FCSTD DOCUMENT  (FreeCAD 0.20R29177 +426 (Git))
Label: assem
License: All rights reserved
LicenseURL: http://en.wikipedia.org/wiki/All_rights_reserved
objects: App::Link×12, App::DocumentObjectGroup×3, PartDesign::CoordinateSystem×1, App::FeaturePython×1, App::Part×1
note: 1 computed .brp shape members not serialized (recipe doc carries the construction recipe); baked Part::Feature solids carry a one-line shape summary decoded from their .brp
EXTERNAL_REF file=house.FCStd obj=LCS_0
EXTERNAL_REF file=house.FCStd obj=house
EXTERNAL_REF file=house.FCStd obj=LCS_chute
EXTERNAL_REF file=seed_chute.FCStd obj=LCS_0
EXTERNAL_REF file=seed_chute.FCStd obj=seed_chute
EXTERNAL_REF file=28BYJ-48_Stepper.FCStd obj=LCS_1
EXTERNAL_REF file=house.FCStd obj=LCS_1
EXTERNAL_REF file=28BYJ-48_Stepper.FCStd obj=_8BYJ_48_Stepper
EXTERNAL_REF file=house.FCStd obj=LCS_2
EXTERNAL_REF file=28BYJ-48_Stepper.FCStd obj=LCS_2
EXTERNAL_REF file=food_rotor.FCStd obj=LCS_1
EXTERNAL_REF file=food_rotor.FCStd obj=food_rotor
EXTERNAL_REF file=ESP32-CAM.FCStd obj=LCS_1
EXTERNAL_REF file=house.FCStd obj=LCS_3
EXTERNAL_REF file=ESP32-CAM.FCStd obj=ESP32_CAM
EXTERNAL_REF file=house.FCStd obj=LCS_roof
EXTERNAL_REF file=roof.FCStd obj=LCS_1
EXTERNAL_REF file=roof.FCStd obj=roof
EXTERNAL_REF file=house.FCStd obj=LCS_4
EXTERNAL_REF file=load_cell.FCStd obj=LCS_1
EXTERNAL_REF file=load_cell.FCStd obj=load_cell
EXTERNAL_REF file=house.FCStd obj=LCS_5
EXTERNAL_REF file=load_cell.FCStd obj=LCS_2
EXTERNAL_REF file=perch.FCStd obj=LCS_1
EXTERNAL_REF file=perch.FCStd obj=perch
EXTERNAL_REF file=back_panel.FCStd obj=LCS_1
EXTERNAL_REF file=house.FCStd obj=LCS_back_panel
EXTERNAL_REF file=back_panel.FCStd obj=back_panel

FEATURE [App::DocumentObjectGroup] Parts
FEATURE [PartDesign::CoordinateSystem] LCS_Origin
  AttacherType = Attacher::AttachEngine3D
  MapMode = 2
  Support = -> [X_Axis]
FEATURE [App::DocumentObjectGroup] Constraints
FEATURE [App::FeaturePython] Variables  # WARN: FeaturePython — macro-defined, semantics opaque (R4)
  Type = App::PropertyContainer
FEATURE [App::DocumentObjectGroup] Configurations
FEATURE [App::Link] house
  AttachedBy = #LCS_0
  AttachedTo = Parent Assembly#LCS_Origin
  LinkedObject = -> <external house.FCStd>#house
  SolverId = Asm4EE
  expr: Placement = LCS_Origin.Placement * AttachmentOffset * house#LCS_0.Placement ^ -1
FEATURE [App::Link] seed_chute
  AttachedBy = #LCS_0
  AttachedTo = house#LCS_chute
  AttachmentOffset = pos=(0,0,0) rot=(0.57735,-0.57735,-0.57735;4.18879rad)
  LinkPlacement = pos=(80,69.282,120) rot=(0,0,-1;3.14159rad)
  LinkedObject = -> <external seed_chute.FCStd>#seed_chute
  Placement = pos=(80,69.282,120) rot=(0,0,-1;3.14159rad)
  SolverId = Asm4EE
  expr: Placement = house.Placement * house#LCS_chute.Placement * AttachmentOffset * seed_chute#LCS_0.Placement ^ -1
FEATURE [App::Link] _8BYJ_48_Stepper001  label="28BYJ-48_Stepper001"
  AttachedBy = #LCS_1
  AttachedTo = house#LCS_1
  AttachmentOffset = pos=(0,0,0) rot=(0,0,1;4.71239rad)
  LinkPlacement = pos=(115.801,55.3109,107) rot=(0.377964,0.654654,0.654654;2.41886rad)
  LinkedObject = -> <external 28BYJ-48_Stepper.FCStd>#_8BYJ_48_Stepper
  Placement = pos=(115.801,55.3109,107) rot=(0.377964,0.654654,0.654654;2.41886rad)
  SolverId = Asm4EE
  expr: Placement = house.Placement * house#LCS_1.Placement * AttachmentOffset * _8BYJ_48_Stepper#LCS_1.Placement ^ -1
FEATURE [App::Link] _8BYJ_48_Stepper001001  label="28BYJ-48_Stepper002"
  AttachedBy = #LCS_1
  AttachedTo = house#LCS_2
  AttachmentOffset = pos=(0,0,0) rot=(0,0,1;1.5708rad)
  LinkPlacement = pos=(44.1987,55.3109,107) rot=(-0.377964,0.654654,0.654654;3.86433rad)
  LinkedObject = -> <external 28BYJ-48_Stepper.FCStd>#_8BYJ_48_Stepper
  Placement = pos=(44.1987,55.3109,107) rot=(-0.377964,0.654654,0.654654;3.86433rad)
  SolverId = Asm4EE
  expr: Placement = house.Placement * house#LCS_2.Placement * AttachmentOffset * _8BYJ_48_Stepper#LCS_1.Placement ^ -1
FEATURE [App::Link] food_rotor
  AttachedBy = #LCS_1
  AttachedTo = _8BYJ_48_Stepper001#LCS_2
  AttachmentOffset = pos=(0,0,0) rot=(1,0,0;3.14159rad)
  LinkPlacement = pos=(97.0384,45.4112,134.509) rot=(-0.448088,-0.776111,0.4437;4.45208rad)
  LinkedObject = -> <external food_rotor.FCStd>#food_rotor
  Placement = pos=(97.0384,45.4112,134.509) rot=(-0.448088,-0.776111,0.4437;4.45208rad)
  SolverId = Asm4EE
  expr: Placement = _8BYJ_48_Stepper001.Placement * _8BYJ_48_Stepper#LCS_2.Placement * AttachmentOffset * food_rotor#LCS_1.Placement ^ -1
FEATURE [App::Link] food_rotor001
  AttachedBy = #LCS_1
  AttachedTo = _8BYJ_48_Stepper001001#LCS_2
  AttachmentOffset = pos=(0,0,0) rot=(0,1,0;3.14159rad)
  LinkPlacement = pos=(62.9616,45.4112,95.4911) rot=(-0.446327,0.773062,-0.450741;4.46732rad)
  LinkedObject = -> <external food_rotor.FCStd>#food_rotor
  Placement = pos=(62.9616,45.4112,95.4911) rot=(-0.446327,0.773062,-0.450741;4.46732rad)
  SolverId = Asm4EE
  expr: Placement = _8BYJ_48_Stepper001001.Placement * _8BYJ_48_Stepper#LCS_2.Placement * AttachmentOffset * food_rotor#LCS_1.Placement ^ -1
FEATURE [App::Link] ESP32_CAM  label="ESP32-CAM"
  AttachedBy = #LCS_1
  AttachedTo = house#LCS_3
  AttachmentOffset = pos=(0,-3,-3) rot=(0,0,1;4.71239rad)
  LinkPlacement = pos=(93.5126,106.07,75.3966) rot=(-0.707107,0,0.707107;3.14159rad)
  LinkedObject = -> <external ESP32-CAM.FCStd>#ESP32_CAM
  Placement = pos=(93.5126,106.07,75.3966) rot=(-0.707107,0,0.707107;3.14159rad)
  SolverId = Asm4EE
  expr: Placement = house.Placement * house#LCS_3.Placement * AttachmentOffset * ESP32_CAM#LCS_1.Placement ^ -1
FEATURE [App::Link] roof
  AttachedBy = #LCS_1
  AttachedTo = house#LCS_roof
  AttachmentOffset = pos=(0,-1,0) rot=(0,0,1;3.14159rad)
  LinkPlacement = pos=(80,160,181) rot=(0,0,1;3.14159rad)
  LinkedObject = -> <external roof.FCStd>#roof
  Placement = pos=(80,160,181) rot=(0,0,1;3.14159rad)
  SolverId = Asm4EE
  expr: Placement = house.Placement * house#LCS_roof.Placement * AttachmentOffset * roof#LCS_1.Placement ^ -1
FEATURE [App::Link] load_cell
  AttachedBy = #LCS_1
  AttachedTo = house#LCS_4
  AttachmentOffset = pos=(0,0,0) rot=(0,-1,0;3.14159rad)
  LinkPlacement = pos=(3.65,-25,1.3) rot=(0,0,1;0rad)
  LinkedObject = -> <external load_cell.FCStd>#load_cell
  Placement = pos=(3.65,-25,1.3) rot=(0,0,1;0rad)
  SolverId = Asm4EE
  expr: Placement = house.Placement * house#LCS_4.Placement * AttachmentOffset * load_cell#LCS_1.Placement ^ -1
FEATURE [App::Link] load_cell001
  AttachedBy = #LCS_1
  AttachedTo = house#LCS_5
  AttachmentOffset = pos=(0,0,0) rot=(0,-1,0;3.14159rad)
  LinkPlacement = pos=(143.65,-25,1.3) rot=(0,0,1;0rad)
  LinkedObject = -> <external load_cell.FCStd>#load_cell
  Placement = pos=(143.65,-25,1.3) rot=(0,0,1;0rad)
  SolverId = Asm4EE
  expr: Placement = house.Placement * house#LCS_5.Placement * AttachmentOffset * load_cell#LCS_1.Placement ^ -1
FEATURE [App::Link] perch
  AttachedBy = #LCS_1
  AttachedTo = load_cell#LCS_2
  LinkPlacement = pos=(3.65,-25,14) rot=(0,0,1;0rad)
  LinkedObject = -> <external perch.FCStd>#perch
  Placement = pos=(3.65,-25,14) rot=(0,0,1;0rad)
  SolverId = Asm4EE
  expr: Placement = load_cell.Placement * load_cell#LCS_2.Placement * AttachmentOffset * perch#LCS_1.Placement ^ -1
FEATURE [App::Link] back_panel
  AttachedBy = #LCS_1
  AttachedTo = house#LCS_back_panel
  AttachmentOffset = pos=(0,0,0) rot=(0,-1,0;3.14159rad)
  LinkPlacement = pos=(6.5,160,6.5) rot=(0,0,1;0rad)
  LinkedObject = -> <external back_panel.FCStd>#back_panel
  Placement = pos=(6.5,160,6.5) rot=(0,0,1;0rad)
  SolverId = Asm4EE
  expr: Placement = house.Placement * house#LCS_back_panel.Placement * AttachmentOffset * back_panel#LCS_1.Placement ^ -1
FEATURE [App::Part] Assembly
  AssemblyType = Part::Link
  Group = -> [LCS_Origin,Constraints,Variables,Configurations,house,seed_chute,_8BYJ_48_Stepper001,_8BYJ_48_Stepper001001,food_rotor,food_rotor001,ESP32_CAM,roof,load_cell,load_cell001,perch,back_panel]
  Origin = -> Origin
  Type = Assembly

RESOLVED EXTERNAL PARTS (link-assembly join: the EXTERNAL_REF files above that resolve inside this repo's crawl, each included once):
---- part back_panel.FCStd = doc fcstd_124646275c1f ----
FCSTD DOCUMENT  (FreeCAD 0.20R29177 +426 (Git))
Label: back_panel
License: All rights reserved
LicenseURL: http://en.wikipedia.org/wiki/All_rights_reserved
objects: Sketcher::SketchObject×3, PartDesign::Pad×2, PartDesign::CoordinateSystem×2, PartDesign::Pocket×1, PartDesign::Body×1, App::Part×1
note: 12 computed .brp shape members not serialized (recipe doc carries the construction recipe); baked Part::Feature solids carry a one-line shape summary decoded from their .brp

FEATURE [Sketcher::SketchObject] Sketch
  FullyConstrained = true
  MapMode = 5
  Placement = pos=(0,0,0) rot=(1,0,0;1.5708rad)
  Support = -> [XZ_Plane]
  sketch-geometry (14):
    g0: LineSegment StartX=-0.5 StartY=-0.5 StartZ=0 EndX=-0.5 EndY=143.5 EndZ=0
    g1: LineSegment StartX=-0.5 StartY=143.5 StartZ=0 EndX=73.5 EndY=163.5 EndZ=0
    g2: LineSegment StartX=73.5 StartY=163.5 StartZ=0 EndX=147.5 EndY=143.5 EndZ=0
    g3: LineSegment StartX=147.5 StartY=143.5 StartZ=0 EndX=147.5 EndY=-0.5 EndZ=0
    g4: LineSegment StartX=147.5 StartY=-0.5 StartZ=0 EndX=-0.5 EndY=-0.5 EndZ=0
    g5: LineSegment StartX=0 StartY=0 StartZ=0 EndX=147 EndY=0 EndZ=0
    g6: LineSegment StartX=147 StartY=0 StartZ=0 EndX=147 EndY=143.135 EndZ=0
    g7: LineSegment StartX=147 StartY=143.135 StartZ=0 EndX=73.5 EndY=163 EndZ=0
    g8: LineSegment StartX=73.5 StartY=163 StartZ=0 EndX=0 EndY=143.135 EndZ=0
    g9: LineSegment StartX=0 StartY=143.135 StartZ=0 EndX=0 EndY=0 EndZ=0
    g10: LineSegment StartX=0 StartY=0 StartZ=0 EndX=0 EndY=-0.5 EndZ=0
    g11: LineSegment StartX=0 StartY=0 StartZ=0 EndX=-0.5 EndY=0 EndZ=0
    g12: LineSegment StartX=147 StartY=143.135 StartZ=0 EndX=147.5 EndY=143.135 EndZ=0
    g13: LineSegment StartX=73.5 StartY=163 StartZ=0 EndX=73.5 EndY=163.5 EndZ=0
  constraints (40):
    c: Coincident(g1,g0)
    c: Coincident(g2,g1)
    c: Coincident(g3,g2)
    c: Vertical(g3)
    c: Coincident(g4,g3)
    c: Horizontal(g4)
    c: DistanceY(g0,g0) = 144
    c: DistanceX(g4,g4) = 148
    c: Equal(g0,g3)
    c: Equal(g2,g1)
    c: DistanceY(g0,g1) = 20
    c: Horizontal(g5)
    c: Coincident(g6,g5)
    c: Vertical(g6)
    c: Coincident(g7,g6)
    c: Coincident(g8,g7)
    c: Coincident(g9,g8)
    c: Coincident(g9,g5)
    c: Vertical(g9)
    c: Coincident(g10,g5)
    c: PointOnObject(g10,g4)
    c: Coincident(g11,g5)
    c: PointOnObject(g11,g0)
    c: Horizontal(g11)
    c: Coincident(g12,g6)
    c: PointOnObject(g12,g3)
    c: Horizontal(g12)
    c: Coincident(g13,g7)
    c: Coincident(g13,g1)
    c: Vertical(g13)
    c: Equal(g12,g13)
    c: Equal(g13,g11)
    c: Equal(g11,g10)
    c: Vertical(g10)
    c: DistanceY(g10,g10) = 0.5
    c: Parallel(g8,g1)
    c: Parallel(g7,g2)
    c: Coincident(g4,g0)
    c: Coincident(g5,g-1)
    c: Vertical(g0)
FEATURE [PartDesign::Pad] Pad
  Direction = (0,-1,-2e-16)
  Length = 4
  Length2 = 10
  Placement = pos=(0,0,0) rot=(1,0,0;1.5708rad)
  Profile = -> Sketch
  ReferenceAxis = -> Sketch [N_Axis]
  Type = 0
FEATURE [Sketcher::SketchObject] Sketch001
  FullyConstrained = true
  MapMode = 5
  Placement = pos=(0,-4,-9e-16) rot=(1,0,0;1.5708rad)
  Support = -> [Pad]
  sketch-geometry (8):
    g0: Circle CenterX=5.5 CenterY=5.5 CenterZ=0 NormalX=0 NormalY=0 NormalZ=1 AngleXU=0 Radius=2.3
    g1: Circle CenterX=141.5 CenterY=5.5 CenterZ=0 NormalX=0 NormalY=0 NormalZ=1 AngleXU=0 Radius=2.3
    g2: Circle CenterX=141.5 CenterY=132.5 CenterZ=0 NormalX=0 NormalY=0 NormalZ=1 AngleXU=0 Radius=2.3
    g3: Circle CenterX=5.5 CenterY=132.5 CenterZ=0 NormalX=0 NormalY=0 NormalZ=1 AngleXU=0 Radius=2.3
    g4: LineSegment StartX=5.5 StartY=132.5 StartZ=0 EndX=141.5 EndY=132.5 EndZ=0
    g5: LineSegment StartX=141.5 StartY=132.5 StartZ=0 EndX=141.5 EndY=5.5 EndZ=0
    g6: LineSegment StartX=141.5 StartY=5.5 StartZ=0 EndX=5.5 EndY=5.5 EndZ=0
    g7: LineSegment StartX=5.5 StartY=5.5 StartZ=0 EndX=5.5 EndY=132.5 EndZ=0
  constraints (20):
    c: Equal(g2,g1)
    c: Equal(g1,g0)
    c: Equal(g0,g3)
    c: Coincident(g4,g5)
    c: Coincident(g5,g6)
    c: Coincident(g6,g7)
    c: Coincident(g7,g4)
    c: Horizontal(g4)
    c: Horizontal(g6)
    c: Vertical(g5)
    c: Vertical(g7)
    c: Coincident(g4,g3)
    c: Coincident(g5,g1)
    c: Coincident(g2,g4)
    c: Coincident(g0,g6)
    c: Diameter(g0) = 4.6
    c: DistanceX(g4,g4) = 136
    c: DistanceY(g7,g7) = 127
    c: DistanceX(g-1,g0) = 5.5
    c: DistanceY(g-1,g0) = 5.5
FEATURE [PartDesign::Pocket] Pocket
  BaseFeature = -> Pad
  Direction = (0,1,2e-16)
  Length = 5
  Length2 = 5
  Placement = pos=(0,0,0) rot=(1,0,0;1.5708rad)
  Profile = -> Sketch001
  ReferenceAxis = -> Sketch001 [N_Axis]
  Type = 0
FEATURE [PartDesign::CoordinateSystem] LCS_0
  AttacherType = Attacher::AttachEngine3D
  MapMode = 2
  Support = -> [X_Axis001]
FEATURE [PartDesign::CoordinateSystem] LCS_1
  AttacherType = Attacher::AttachEngine3D
  MapMode = 11
  Placement = pos=(5.5,-4,5.5) rot=(-0.57735,0.57735,-0.57735;4.18879rad)
  Support = -> [Pocket]
FEATURE [Sketcher::SketchObject] Sketch002
  FullyConstrained = true
  MapMode = 5
  Placement = pos=(0,0,0) rot=(-1,0,0;1.5708rad)
  Support = -> [Pocket]
  sketch-geometry (1):
    g0: Circle CenterX=73.5 CenterY=-140 CenterZ=0 NormalX=0 NormalY=0 NormalZ=1 AngleXU=0 Radius=5
  constraints (3):
    c: Diameter(g0) = 10
    c: DistanceX(g-1,g0) = 73.5
    c: DistanceY(g0,g-1) = 140
FEATURE [PartDesign::Pad] Pad001
  BaseFeature = -> Pocket
  Direction = (0,1,2e-16)
  Length = 10
  Length2 = 10
  Placement = pos=(0,0,0) rot=(1,0,0;1.5708rad)
  Profile = -> Sketch002
  ReferenceAxis = -> Sketch002 [N_Axis]
  Type = 0
FEATURE [PartDesign::Body] Body
  Group = -> [Sketch,Pad,Sketch001,Pocket,Sketch002,Pad001]
  Origin = -> Origin
  Tip = -> Pad001
FEATURE [App::Part] back_panel
  Group = -> [LCS_0,Body,LCS_1]
  Origin = -> Origin001
---- part food_rotor.FCStd = doc fcstd_7d18d374bac9 ----
FCSTD DOCUMENT  (FreeCAD 0.20R29177 +426 (Git))
Label: food_rotor
License: All rights reserved
LicenseURL: http://en.wikipedia.org/wiki/All_rights_reserved
objects: Sketcher::SketchObject×3, PartDesign::Pad×2, PartDesign::CoordinateSystem×2, PartDesign::Pocket×1, PartDesign::Body×1, App::Part×1
note: 12 computed .brp shape members not serialized (recipe doc carries the construction recipe); baked Part::Feature solids carry a one-line shape summary decoded from their .brp

FEATURE [Sketcher::SketchObject] Sketch
  FullyConstrained = true
  MapMode = 5
  Support = -> [XY_Plane]
  sketch-geometry (4):
    g0: LineSegment StartX=0 StartY=0 StartZ=0 EndX=39 EndY=0 EndZ=0
    g1: LineSegment StartX=39 StartY=0 StartZ=0 EndX=39 EndY=14 EndZ=0
    g2: LineSegment StartX=39 StartY=14 StartZ=0 EndX=0 EndY=14 EndZ=0
    g3: LineSegment StartX=0 StartY=14 StartZ=0 EndX=0 EndY=0 EndZ=0
  constraints (11):
    c: Coincident(g0,g1)
    c: Coincident(g1,g2)
    c: Coincident(g2,g3)
    c: Coincident(g3,g0)
    c: Horizontal(g0)
    c: Horizontal(g2)
    c: Vertical(g1)
    c: Vertical(g3)
    c: Coincident(g0,g-1)
    c: DistanceX(g2,g2) = 39
    c: DistanceY(g1,g1) = 14
FEATURE [PartDesign::Pad] Pad
  Direction = (0,0,1)
  Length = 2
  Length2 = 10
  Profile = -> Sketch
  ReferenceAxis = -> Sketch [N_Axis]
  Type = 0
FEATURE [Sketcher::SketchObject] Sketch001
  FullyConstrained = true
  MapMode = 5
  Placement = pos=(0,0,0) rot=(1,0,0;1.5708rad)
  Support = -> [Pad]
  sketch-geometry (1):
    g0: Circle CenterX=19.5 CenterY=1 CenterZ=0 NormalX=0 NormalY=0 NormalZ=1 AngleXU=0 Radius=5
  constraints (3):
    c: DistanceY(g-1,g0) = 1
    c: DistanceX(g-1,g0) = 19.5
    c: Diameter(g0) = 10
FEATURE [PartDesign::Pad] Pad001
  BaseFeature = -> Pad
  Direction = (0,-1,2e-16)
  Length = 17.199
  Length2 = 10
  Profile = -> Sketch001
  ReferenceAxis = -> Sketch001 [N_Axis]
  Reversed = true
  Type = 0
FEATURE [Sketcher::SketchObject] Sketch002
  FullyConstrained = true
  MapMode = 5
  Placement = pos=(0,17.199,-3.8e-15) rot=(0,0.707107,0.707107;3.14159rad)
  Support = -> [Pad001]
  sketch-geometry (4):
    g0: ArcOfCircle CenterX=-19.5 CenterY=1 CenterZ=0 NormalX=0 NormalY=0 NormalZ=1 AngleXU=0 Radius=2.55 StartAngle=2.48825 EndAngle=3.79493
    g1: ArcOfCircle CenterX=-19.5 CenterY=1 CenterZ=0 NormalX=0 NormalY=0 NormalZ=1 AngleXU=0 Radius=2.55 StartAngle=5.62984 EndAngle=6.93653
    g2: LineSegment StartX=-21.5248 StartY=2.55 StartZ=0 EndX=-17.4752 EndY=2.55 EndZ=0
    g3: LineSegment StartX=-17.4752 StartY=-0.55 StartZ=0 EndX=-21.5248 EndY=-0.55 EndZ=0
  constraints (13):
    c: Coincident(g1,g0)
    c: Coincident(g2,g0)
    c: Coincident(g2,g1)
    c: Coincident(g3,g1)
    c: Coincident(g3,g0)
    c: Horizontal(g3)
    c: Horizontal(g2)
    c: Equal(g2,g3)
    c: Equal(g0,g1)
    c: Diameter(g1) = 5.1
    c: DistanceY(g1,g1) = 3.1
    c: DistanceY(g-1,g0) = 1
    c: DistanceX(g0,g-1) = 19.5
FEATURE [PartDesign::Pocket] Pocket
  BaseFeature = -> Pad001
  Direction = (0,-1,2e-16)
  Length = 8
  Length2 = 5
  Profile = -> Sketch002
  ReferenceAxis = -> Sketch002 [N_Axis]
  Type = 0
FEATURE [PartDesign::Body] Body
  Group = -> [Sketch,Pad,Sketch001,Pad001,Sketch002,Pocket]
  Origin = -> Origin
  Tip = -> Pocket
FEATURE [PartDesign::CoordinateSystem] LCS_0
  AttacherType = Attacher::AttachEngine3D
  MapMode = 2
  Support = -> [X_Axis001]
FEATURE [PartDesign::CoordinateSystem] LCS_1
  AttacherType = Attacher::AttachEngine3D
  MapMode = 11
  Placement = pos=(19.5,17.199,1) rot=(-0.819836,0.404888,0.404888;1.76815rad)
  Support = -> [Pocket]
FEATURE [App::Part] food_rotor
  Group = -> [LCS_0,Body,LCS_1]
  Origin = -> Origin001
---- part house.FCStd = doc fcstd_4f1505ac3fc7 ----
FCSTD DOCUMENT  (FreeCAD 0.20R29177 +426 (Git))
Label: house
License: All rights reserved
LicenseURL: http://en.wikipedia.org/wiki/All_rights_reserved
objects: Sketcher::SketchObject×19, PartDesign::Pocket×14, PartDesign::CoordinateSystem×10, PartDesign::Pad×5, PartDesign::Fillet×1, PartDesign::Body×1, App::Part×1
note: 70 computed .brp shape members not serialized (recipe doc carries the construction recipe); baked Part::Feature solids carry a one-line shape summary decoded from their .brp

FEATURE [Sketcher::SketchObject] Sketch
  FullyConstrained = true
  MapMode = 5
  Placement = pos=(0,0,0) rot=(1,0,0;1.5708rad)
  Support = -> [XZ_Plane]
  sketch-geometry (5):
    g0: LineSegment StartX=0 StartY=0 StartZ=0 EndX=0 EndY=180 EndZ=0
    g1: LineSegment StartX=0 StartY=0 StartZ=0 EndX=160 EndY=0 EndZ=0
    g2: LineSegment StartX=160 StartY=0 StartZ=0 EndX=160 EndY=180 EndZ=0
    g3: LineSegment StartX=160 StartY=180 StartZ=0 EndX=80 EndY=200 EndZ=0
    g4: LineSegment StartX=80 StartY=200 StartZ=0 EndX=0 EndY=180 EndZ=0
  constraints (14):
    c: Coincident(g0,g-1)
    c: PointOnObject(g0,g-2)
    c: Coincident(g1,g0)
    c: PointOnObject(g1,g-1)
    c: Coincident(g2,g1)
    c: Vertical(g2)
    c: Coincident(g3,g2)
    c: Coincident(g4,g3)
    c: Coincident(g4,g0)
    c: Equal(g3,g4)
    c: Equal(g2,g0)
    c: DistanceY(g0,g3) = 200
    c: DistanceX(g1,g1) = 160
    c: DistanceY(g0,g0) = 180
FEATURE [PartDesign::Pad] Pad
  Direction = (0,-1,-2e-16)
  Length = 160
  Length2 = 10
  Placement = pos=(0,0,0) rot=(1,0,0;1.5708rad)
  Profile = -> Sketch
  ReferenceAxis = -> Sketch [N_Axis]
  Reversed = true
  Type = 0
FEATURE [Sketcher::SketchObject] Sketch001
  FullyConstrained = true
  MapMode = 5
  Placement = pos=(0,-2e-16,0) rot=(1,0,0;1.5708rad)
  Support = -> [Pad]
  sketch-geometry (4):
    g0: LineSegment StartX=20 StartY=110 StartZ=0 EndX=140 EndY=110 EndZ=0
    g1: LineSegment StartX=140 StartY=110 StartZ=0 EndX=140 EndY=20 EndZ=0
    g2: LineSegment StartX=140 StartY=20 StartZ=0 EndX=20 EndY=20 EndZ=0
    g3: LineSegment StartX=20 StartY=20 StartZ=0 EndX=20 EndY=110 EndZ=0
  constraints (12):
    c: Coincident(g0,g1)
    c: Coincident(g1,g2)
    c: Coincident(g2,g3)
    c: Coincident(g3,g0)
    c: Horizontal(g0)
    c: Horizontal(g2)
    c: Vertical(g1)
    c: Vertical(g3)
    c: DistanceX(g2,g2) = 120
    c: DistanceY(g-1,g2) = 20
    c: DistanceX(g-1,g2) = 20
    c: DistanceY(g3,g3) = 90
FEATURE [PartDesign::Pocket] Pocket
  BaseFeature = -> Pad
  Direction = (0,1,2e-16)
  Length = 100
  Length2 = 5
  Placement = pos=(0,0,0) rot=(1,0,0;1.5708rad)
  Profile = -> Sketch001
  ReferenceAxis = -> Sketch001 [N_Axis]
  Type = 0
FEATURE [Sketcher::SketchObject] Sketch002
  FullyConstrained = true
  MapMode = 5
  Placement = pos=(0,4.4e-15,20) rot=(0,0,1;3.14159rad)
  Support = -> [Pocket]
  sketch-geometry (6):
    g0: LineSegment StartX=-20 StartY=0 StartZ=0 EndX=-76 EndY=-96.9948 EndZ=0
    g1: LineSegment StartX=-140 StartY=0 StartZ=0 EndX=-84 EndY=-96.9948 EndZ=0
    g2: LineSegment StartX=-84 StartY=-96.9948 StartZ=0 EndX=-76 EndY=-96.9948 EndZ=0
    g3: LineSegment StartX=-140 StartY=0 StartZ=0 EndX=-140 EndY=-100 EndZ=0
    g4: LineSegment StartX=-140 StartY=-100 StartZ=0 EndX=-20 EndY=-100 EndZ=0
    g5: LineSegment StartX=-20 StartY=-100 StartZ=0 EndX=-20 EndY=0 EndZ=0
  constraints (18):
    c: PointOnObject(g0,g-1)
    c: PointOnObject(g1,g-1)
    c: DistanceX(g0,g-1) = 20
    c: DistanceX(g1,g0) = 120
    c: Coincident(g2,g1)
    c: Coincident(g2,g0)
    c: Horizontal(g2)
    c: Coincident(g4,g3)
    c: Horizontal(g4)
    c: Coincident(g5,g4)
    c: Vertical(g5)
    c: Vertical(g3)
    c: Equal(g1,g0)
    c: DistanceX(g2,g2) = 8
    c: Angle(g4,g0) = 1.0472
    c: DistanceY(g5,g5) = 100
    c: Coincident(g1,g3)
    c: Coincident(g0,g5)
FEATURE [PartDesign::Pad] Pad001
  BaseFeature = -> Pocket
  Direction = (0,-2e-16,1)
  Length = 90
  Length2 = 10
  Placement = pos=(0,0,0) rot=(1,0,0;1.5708rad)
  Profile = -> Sketch002
  ReferenceAxis = -> Sketch002 [N_Axis]
  Type = 0
FEATURE [Sketcher::SketchObject] Sketch003
  FullyConstrained = true
  MapMode = 5
  Placement = pos=(0,4.4e-15,20) rot=(0,0,1;3.14159rad)
  Support = -> [Pad001]
  sketch-geometry (7):
    g0: LineSegment StartX=-21.7321 StartY=-3 StartZ=0 EndX=-138.268 EndY=-3 EndZ=0
    g1: LineSegment StartX=-138.268 StartY=-3 StartZ=0 EndX=-84 EndY=-96.9948 EndZ=0
    g2: LineSegment StartX=-84 StartY=-96.9948 StartZ=0 EndX=-76 EndY=-96.9948 EndZ=0
    g3: LineSegment StartX=-76 StartY=-96.9948 StartZ=0 EndX=-21.7321 EndY=-3 EndZ=0
    g4: GeomPoint X=-80 Y=-3 Z=0
    g5: LineSegment StartX=-138.268 StartY=-3 StartZ=0 EndX=-140 EndY=0 EndZ=0
    g6: LineSegment StartX=-21.7321 StartY=-3 StartZ=0 EndX=-20 EndY=0 EndZ=0
  constraints (19):
    c: Horizontal(g0)
    c: Coincident(g1,g0)
    c: Coincident(g2,g1)
    c: Horizontal(g2)
    c: Coincident(g3,g2)
    c: Equal(g3,g1)
    c: Symmetric(g0,g0,g4)
    c: DistanceX(g4,g-1) = 80
    c: DistanceX(g2,g2) = 8
    c: Coincident(g0,g3)
    c: Angle(g3,g-1) = 2.0944
    c: DistanceY(g0,g-1) = 3
    c: Coincident(g5,g0)
    c: PointOnObject(g5,g-1)
    c: Coincident(g6,g0)
    c: PointOnObject(g6,g-1)
    c: Parallel(g3,g6)
    c: Parallel(g1,g5)
    c: DistanceX(g5,g6) = 120
FEATURE [PartDesign::Pocket] Pocket001
  BaseFeature = -> Pad001
  Direction = (0,2e-16,-1)
  Length = 16
  Length2 = 5
  Placement = pos=(0,0,0) rot=(1,0,0;1.5708rad)
  Profile = -> Sketch003
  ReferenceAxis = -> Sketch003 [N_Axis]
  Type = 0
FEATURE [Sketcher::SketchObject] Sketch004
  FullyConstrained = true
  MapMode = 5
  Placement = pos=(0,160,-3e-16) rot=(-1,0,0;1.5708rad)
  Support = -> [Pocket001]
  sketch-geometry (5):
    g0: LineSegment StartX=6 StartY=-150 StartZ=0 EndX=6 EndY=-6 EndZ=0
    g1: LineSegment StartX=6 StartY=-6 StartZ=0 EndX=154 EndY=-6 EndZ=0
    g2: LineSegment StartX=154 StartY=-6 StartZ=0 EndX=154 EndY=-150 EndZ=0
    g3: LineSegment StartX=154 StartY=-150 StartZ=0 EndX=80 EndY=-170 EndZ=0
    g4: LineSegment StartX=80 StartY=-170 StartZ=0 EndX=6 EndY=-150 EndZ=0
  constraints (15):
    c: Coincident(g0,g1)
    c: Coincident(g1,g2)
    c: Horizontal(g1)
    c: Vertical(g0)
    c: Vertical(g2)
    c: DistanceY(g0,g-1) = 150
    c: DistanceY(g0,g-1) = 6
    c: DistanceX(g-1,g0) = 6
    c: DistanceX(g1,g1) = 148
    c: Coincident(g3,g2)
    c: Coincident(g4,g3)
    c: Coincident(g4,g0)
    c: Equal(g3,g4)
    c: DistanceY(g3,g0) = 20
    c: Horizontal(g0,g2)
FEATURE [PartDesign::Pocket] Pocket002
  BaseFeature = -> Pocket001
  Direction = (0,-1,-2e-16)
  Length = 60
  Length2 = 5
  Placement = pos=(0,0,0) rot=(1,0,0;1.5708rad)
  Profile = -> Sketch004
  ReferenceAxis = -> Sketch004 [N_Axis]
  Type = 0
FEATURE [Sketcher::SketchObject] Sketch006
  AttachmentOffset = pos=(0,0,200) rot=(0,0,1;0rad)
  FullyConstrained = true
  MapMode = 5
  Placement = pos=(0,0,200) rot=(0,0,1;0rad)
  Support = -> [XY_Plane]
  sketch-geometry (4):
    g0: LineSegment StartX=6 StartY=154 StartZ=0 EndX=154 EndY=154 EndZ=0
    g1: LineSegment StartX=154 StartY=154 StartZ=0 EndX=154 EndY=6 EndZ=0
    g2: LineSegment StartX=154 StartY=6 StartZ=0 EndX=6 EndY=6 EndZ=0
    g3: LineSegment StartX=6 StartY=6 StartZ=0 EndX=6 EndY=154 EndZ=0
  constraints (12):
    c: Coincident(g0,g1)
    c: Coincident(g1,g2)
    c: Coincident(g2,g3)
    c: Coincident(g3,g0)
    c: Horizontal(g0)
    c: Horizontal(g2)
    c: Vertical(g1)
    c: Vertical(g3)
    c: DistanceX(g-1,g2) = 6
    c: DistanceY(g-1,g2) = 6
    c: DistanceX(g0,g0) = 148
    c: DistanceY(g3,g3) = 148
FEATURE [PartDesign::Pocket] Pocket004
  BaseFeature = -> Pocket002
  Direction = (0,0,-1)
  Length = 80
  Length2 = 5
  Placement = pos=(0,0,0) rot=(1,0,0;1.5708rad)
  Profile = -> Sketch006
  ReferenceAxis = -> Sketch006 [N_Axis]
  Type = 0
FEATURE [Sketcher::SketchObject] Sketch007
  ExternalGeometry = -> [Pocket004]
  FullyConstrained = true
  MapMode = 5
  Placement = pos=(0,-2e-16,0) rot=(1,0,0;1.5708rad)
  Support = -> [Pocket004]
  sketch-geometry (9):
    g0: LineSegment StartX=3 StartY=16 StartZ=0 EndX=17 EndY=16 EndZ=0
    g1: LineSegment StartX=17 StartY=16 StartZ=0 EndX=17 EndY=0 EndZ=0
    g2: LineSegment StartX=17 StartY=0 StartZ=0 EndX=3 EndY=0 EndZ=0
    g3: LineSegment StartX=3 StartY=0 StartZ=0 EndX=3 EndY=16 EndZ=0
    g4: LineSegment StartX=143 StartY=16 StartZ=0 EndX=157 EndY=16 EndZ=0
    g5: LineSegment StartX=157 StartY=16 StartZ=0 EndX=157 EndY=8.51283e-11 EndZ=0
    g6: LineSegment StartX=157 StartY=8.51283e-11 StartZ=0 EndX=143 EndY=8.51283e-11 EndZ=0
    g7: LineSegment StartX=143 StartY=8.51283e-11 StartZ=0 EndX=143 EndY=16 EndZ=0
    g8: LineSegment StartX=160 StartY=0 StartZ=0 EndX=160 EndY=16 EndZ=0
  constraints (28):
    c: Coincident(g0,g1)
    c: Coincident(g1,g2)
    c: Coincident(g2,g3)
    c: Coincident(g3,g0)
    c: Horizontal(g0)
    c: Horizontal(g2)
    c: Vertical(g1)
    c: Vertical(g3)
    c: DistanceX(g2,g2) = 14
    c: DistanceY(g3,g3) = 16
    c: Coincident(g4,g5)
    c: Coincident(g5,g6)
    c: Coincident(g6,g7)
    c: Coincident(g7,g4)
    c: Horizontal(g4)
    c: Horizontal(g6)
    c: Vertical(g5)
    c: Vertical(g7)
    c: Equal(g4,g0)
    c: Equal(g1,g7)
    c: Horizontal(g4,g0)
    c: DistanceX(g-1,g2) = 3
    c: PointOnObject(g8,g-1)
    c: Vertical(g8)
    c: DistanceX(g-1,g8) = 160
    c: DistanceX(g5,g8) = 3
    c: Horizontal(g4,g8)
    c: PointOnObject(g2,g-1)
FEATURE [PartDesign::Pocket] Pocket005
  BaseFeature = -> Pocket004
  Direction = (0,1,2e-16)
  Length = 100
  Length2 = 5
  Placement = pos=(0,0,0) rot=(1,0,0;1.5708rad)
  Profile = -> Sketch007
  ReferenceAxis = -> Sketch007 [N_Axis]
  Type = 0
FEATURE [Sketcher::SketchObject] Sketch008
  FullyConstrained = true
  MapMode = 5
  Placement = pos=(0,3.6e-15,16) rot=(1,0,0;3.14159rad)
  Support = -> [Pocket005]
  sketch-geometry (22):
    g0: LineSegment StartX=3.65 StartY=25 StartZ=0 EndX=16.35 EndY=25 EndZ=0
    g1: LineSegment StartX=16.35 StartY=25 StartZ=0 EndX=16.35 EndY=-50 EndZ=0
    g2: LineSegment StartX=16.35 StartY=-50 StartZ=0 EndX=3.65 EndY=-50 EndZ=0
    g3: LineSegment StartX=3.65 StartY=-50 StartZ=0 EndX=3.65 EndY=25 EndZ=0
    g4: LineSegment StartX=10 StartY=25 StartZ=0 EndX=10 EndY=-50 EndZ=0
    g5: LineSegment StartX=16.35 StartY=-12.5 StartZ=0 EndX=3.65 EndY=-12.5 EndZ=0
    g6: GeomPoint X=10 Y=-12.5 Z=0
    g7: GeomPoint X=10 Y=-44.5 Z=0
    g8: GeomPoint X=10 Y=-34.5 Z=0
    g9: LineSegment StartX=3 StartY=-24.5 StartZ=0 EndX=17 EndY=-24.5 EndZ=0
    g10: LineSegment StartX=17 StartY=-24.5 StartZ=0 EndX=17 EndY=-54.5 EndZ=0
    g11: LineSegment StartX=17 StartY=-54.5 StartZ=0 EndX=3 EndY=-54.5 EndZ=0
    g12: LineSegment StartX=3 StartY=-54.5 StartZ=0 EndX=3 EndY=-24.5 EndZ=0
    g13: GeomPoint X=10 Y=-54.5 Z=0
    g14: GeomPoint X=10 Y=-39.5 Z=0
    g15: GeomPoint X=10 Y=-24.5 Z=0
    g16: LineSegment StartX=143 StartY=-24.5 StartZ=0 EndX=157 EndY=-24.5 EndZ=0
    g17: LineSegment StartX=157 StartY=-24.5 StartZ=0 EndX=157 EndY=-54.5 EndZ=0
    g18: LineSegment StartX=157 StartY=-54.5 StartZ=0 EndX=143 EndY=-54.5 EndZ=0
    g19: LineSegment StartX=143 StartY=-54.5 StartZ=0 EndX=143 EndY=-24.5 EndZ=0
    g20: GeomPoint X=160 Y=0 Z=0
    g21: GeomPoint X=150 Y=-24.5 Z=0
  constraints (54):
    c: Coincident(g0,g1)
    c: Coincident(g1,g2)
    c: Coincident(g2,g3)
    c: Coincident(g3,g0)
    c: Horizontal(g0)
    c: Horizontal(g2)
    c: Vertical(g1)
    c: Vertical(g3)
    c: PointOnObject(g4,g2)
    c: Vertical(g4)
    c: PointOnObject(g5,g3)
    c: Horizontal(g5)
    c: PointOnObject(g6,g5)
    c: PointOnObject(g6,g4)
    c: Symmetric(g0,g0,g4)
    c: Symmetric(g0,g1,g5)
    c: DistanceY(g3,g3) = 75
    c: DistanceX(g0,g0) = 12.7
    c: DistanceY(g-1,g0) = 25
    c: DistanceX(g-1,g4) = 10
    c: PointOnObject(g7,g4)
    c: PointOnObject(g8,g4)
    c: DistanceY(g8,g5) = 22
    c: DistanceY(g7,g8) = 10
    c: Coincident(g9,g10)
    c: Coincident(g10,g11)
    c: Coincident(g11,g12)
    c: Coincident(g12,g9)
    c: Horizontal(g9)
    c: Horizontal(g11)
    c: Vertical(g10)
    c: Vertical(g12)
    c: DistanceY(g10,g10) = 30
    c: DistanceX(g9,g9) = 14
    c: Symmetric(g11,g10,g13)
    c: PointOnObject(g13,g4)
    c: Symmetric(g8,g7,g14)
    c: PointOnObject(g15,g9)
    c: Symmetric(g15,g13,g14)
    c: Coincident(g16,g17)
    c: Coincident(g17,g18)
    c: Coincident(g18,g19)
    c: Coincident(g19,g16)
    c: Horizontal(g16)
    c: Horizontal(g18)
    c: Vertical(g17)
    c: Vertical(g19)
    c: Equal(g16,g9)
    c: Equal(g10,g19)
    c: Horizontal(g16,g9)
    c: PointOnObject(g20,g-1)
    c: DistanceX(g-1,g20) = 160
    c: Symmetric(g16,g16,g21)
    c: DistanceX(g21,g20) = 10
FEATURE [PartDesign::Pad] Pad002
  BaseFeature = -> Pocket005
  Direction = (0,2e-16,-1)
  Length = 2
  Length2 = 10
  Placement = pos=(0,0,0) rot=(1,0,0;1.5708rad)
  Profile = -> Sketch008
  ReferenceAxis = -> Sketch008 [N_Axis]
  Type = 0
FEATURE [Sketcher::SketchObject] Sketch010
  FullyConstrained = true
  MapMode = 5
  Placement = pos=(0,2.4e-14,110) rot=(1,0,0;3.14159rad)
  sketch-geometry (11):
    g0: LineSegment StartX=40 StartY=-34.641 StartZ=0 EndX=60 EndY=-69.282 EndZ=0
    g1: LineSegment StartX=60 StartY=-69.282 StartZ=0 EndX=72.9904 EndY=-61.782 EndZ=0
    g2: LineSegment StartX=72.9904 StartY=-61.782 StartZ=0 EndX=52.9904 EndY=-27.141 EndZ=0
    g3: LineSegment StartX=52.9904 StartY=-27.141 StartZ=0 EndX=40 EndY=-34.641 EndZ=0
    g4: LineSegment StartX=20 StartY=0 StartZ=0 EndX=60 EndY=-69.282 EndZ=0
    g5: LineSegment StartX=107.01 StartY=-27.141 StartZ=0 EndX=87.0096 EndY=-61.782 EndZ=0
    g6: LineSegment StartX=87.0096 StartY=-61.782 StartZ=0 EndX=100 EndY=-69.282 EndZ=0
    g7: LineSegment StartX=100 StartY=-69.282 StartZ=0 EndX=120 EndY=-34.641 EndZ=0
    g8: LineSegment StartX=120 StartY=-34.641 StartZ=0 EndX=107.01 EndY=-27.141 EndZ=0
    g9: LineSegment StartX=120 StartY=-34.641 StartZ=0 EndX=140 EndY=0 EndZ=0
    g10: GeomPoint X=110 Y=-51.9615 Z=0
  constraints (31):
    c: Coincident(g1,g0)
    c: Coincident(g2,g1)
    c: Coincident(g3,g2)
    c: Coincident(g3,g0)
    c: Perpendicular(g3,g2)
    c: Parallel(g2,g0)
    c: Parallel(g3,g1)
    c: PointOnObject(g4,g-1)
    c: DistanceX(g-1,g4) = 20
    c: Angle(g-1,g4) = 2.0944
    c: PointOnObject(g0,g4)
    c: Distance(g3) = 15
    c: Distance(g2) = 40
    c: Distance(g0,g4) = 40
    c: Coincident(g4,g0)
    c: Coincident(g6,g5)
    c: Coincident(g7,g6)
    c: Coincident(g8,g7)
    c: Coincident(g8,g5)
    c: Parallel(g8,g6)
    c: Parallel(g7,g5)
    c: Perpendicular(g5,g6)
    c: Coincident(g9,g7)
    c: PointOnObject(g9,g-1)
    c: Parallel(g7,g9)
    c: Angle(g-1,g9) = 1.0472
    c: Equal(g5,g2)
    c: Equal(g1,g6)
    c: DistanceX(g4,g9) = 120
    c: Horizontal(g1,g5)
    c: Symmetric(g6,g7,g10)
FEATURE [PartDesign::Pocket] Pocket008
  BaseFeature = -> Pad002
  Direction = (0,0,1)
  Length = 10
  Length2 = 5
  Placement = pos=(0,0,0) rot=(1,0,0;1.5708rad)
  Profile = -> Sketch010
  ReferenceAxis = -> Sketch010 [N_Axis]
  Type = 0
FEATURE [Sketcher::SketchObject] Sketch011
  FullyConstrained = true
  MapMode = 5
  Placement = pos=(0,2.66e-14,120) rot=(0,0,1;3.14159rad)
  Support = -> [Pocket008]
  sketch-geometry (10):
    g0: LineSegment StartX=-130.415 StartY=-30 StartZ=0 EndX=-90 EndY=-100 EndZ=0
    g1: LineSegment StartX=-29.5855 StartY=-30 StartZ=0 EndX=-70 EndY=-100 EndZ=0
    g2: LineSegment StartX=-70 StartY=-100 StartZ=0 EndX=-6 EndY=-100 EndZ=0
    g3: LineSegment StartX=-90 StartY=-100 StartZ=0 EndX=-154 EndY=-100 EndZ=0
    g4: GeomPoint X=-80 Y=0 Z=0
    g5: LineSegment StartX=-80 StartY=0 StartZ=0 EndX=-80 EndY=-160 EndZ=0
    g6: LineSegment StartX=-130.415 StartY=-30 StartZ=0 EndX=-154 EndY=-30 EndZ=0
    g7: LineSegment StartX=-154 StartY=-30 StartZ=0 EndX=-154 EndY=-100 EndZ=0
    g8: LineSegment StartX=-6 StartY=-100 StartZ=0 EndX=-6 EndY=-30 EndZ=0
    g9: LineSegment StartX=-6 StartY=-30 StartZ=0 EndX=-29.5855 EndY=-30 EndZ=0
  constraints (28):
    c: Coincident(g2,g1)
    c: Coincident(g3,g0)
    c: Horizontal(g3)
    c: Horizontal(g2)
    c: Equal(g2,g3)
    c: Horizontal(g1,g0)
    c: DistanceY(g2,g-1) = 100
    c: PointOnObject(g4,g-1)
    c: DistanceX(g4,g-1) = 80
    c: Coincident(g5,g4)
    c: DistanceY(g5,g5) = 160
    c: Angle(g2,g1) = 1.0472
    c: Symmetric(g0,g1,g5)
    c: DistanceX(g0,g1) = 20
    c: Coincident(g6,g0)
    c: Horizontal(g6)
    c: Coincident(g7,g6)
    c: Vertical(g7)
    c: Coincident(g3,g7)
    c: Coincident(g8,g2)
    c: Vertical(g8)
    c: Coincident(g9,g8)
    c: Coincident(g9,g1)
    c: Horizontal(g9)
    c: Equal(g7,g8)
    c: Equal(g9,g6)
    c: DistanceY(g7,g7) = 70
    c: DistanceX(g3,g2) = 148
FEATURE [PartDesign::Pocket] Pocket009
  BaseFeature = -> Pocket008
  Direction = (0,0,-1)
  Length = 50
  Length2 = 5
  Placement = pos=(0,0,0) rot=(1,0,0;1.5708rad)
  Profile = -> Sketch011
  ReferenceAxis = -> Sketch011 [N_Axis]
  Type = 0
FEATURE [Sketcher::SketchObject] Sketch005  label="camera_hole"
  FullyConstrained = true
  MapMode = 5
  Placement = pos=(0,96.9948,-2.15e-14) rot=(1,0,0;1.5708rad)
  Support = -> [Pocket009]
  sketch-geometry (7):
    g0: LineSegment StartX=76 StartY=69 StartZ=0 EndX=84 EndY=69 EndZ=0
    g1: LineSegment StartX=84 StartY=69 StartZ=0 EndX=84 EndY=53 EndZ=0
    g2: LineSegment StartX=84 StartY=53 StartZ=0 EndX=76 EndY=53 EndZ=0
    g3: LineSegment StartX=76 StartY=53 StartZ=0 EndX=76 EndY=69 EndZ=0
    g4: LineSegment StartX=76 StartY=61 StartZ=0 EndX=84 EndY=61 EndZ=0
    g5: LineSegment StartX=76 StartY=65 StartZ=0 EndX=84 EndY=65 EndZ=0
    g6: GeomPoint X=80 Y=53 Z=0
  constraints (19):
    c: Coincident(g0,g1)
    c: Coincident(g1,g2)
    c: Coincident(g2,g3)
    c: Coincident(g3,g0)
    c: Horizontal(g0)
    c: Horizontal(g2)
    c: Vertical(g1)
    c: Vertical(g3)
    c: DistanceX(g0,g0) = 8
    c: PointOnObject(g4,g3)
    c: Horizontal(g4)
    c: PointOnObject(g5,g3)
    c: Horizontal(g5)
    c: Symmetric(g0,g1,g4)
    c: Symmetric(g0,g4,g5)
    c: DistanceY(g-1,g5) = 65
    c: DistanceY(g3,g3) = 16
    c: Symmetric(g2,g1,g6)
    c: DistanceX(g-1,g6) = 80
FEATURE [Sketcher::SketchObject] Sketch009
  FullyConstrained = true
  MapMode = 5
  Placement = pos=(0,1.4e-15,14) rot=(1,0,0;3.14159rad)
  Support = -> [Pocket009]
  sketch-geometry (14):
    g0: LineSegment StartX=3.65 StartY=25 StartZ=0 EndX=16.35 EndY=25 EndZ=0
    g1: LineSegment StartX=16.35 StartY=25 StartZ=0 EndX=16.35 EndY=-50 EndZ=0
    g2: LineSegment StartX=16.35 StartY=-50 StartZ=0 EndX=3.65 EndY=-50 EndZ=0
    g3: LineSegment StartX=3.65 StartY=-50 StartZ=0 EndX=3.65 EndY=25 EndZ=0
    g4: LineSegment StartX=3.65 StartY=-12.5 StartZ=0 EndX=16.35 EndY=-12.5 EndZ=0
    g5: LineSegment StartX=10 StartY=25 StartZ=0 EndX=10 EndY=-50 EndZ=0
    g6: GeomPoint X=10 Y=-12.5 Z=0
    g7: GeomPoint X=10 Y=-44.5 Z=0
    g8: GeomPoint X=10 Y=-34.5 Z=0
    g9: Circle CenterX=10 CenterY=-34.5 CenterZ=0 NormalX=0 NormalY=0 NormalZ=1 AngleXU=0 Radius=2.5
    g10: Circle CenterX=10 CenterY=-44.5 CenterZ=0 NormalX=0 NormalY=0 NormalZ=1 AngleXU=0 Radius=2.5
    g11: Circle CenterX=150 CenterY=-34.5 CenterZ=0 NormalX=0 NormalY=0 NormalZ=1 AngleXU=0 Radius=2.5
    g12: Circle CenterX=150 CenterY=-44.5 CenterZ=0 NormalX=0 NormalY=0 NormalZ=1 AngleXU=0 Radius=2.5
    g13: GeomPoint X=160 Y=0 Z=0
  constraints (36):
    c: Coincident(g0,g1)
    c: Coincident(g1,g2)
    c: Coincident(g2,g3)
    c: Coincident(g3,g0)
    c: Horizontal(g0)
    c: Horizontal(g2)
    c: Vertical(g1)
    c: Vertical(g3)
    c: PointOnObject(g4,g3)
    c: Horizontal(g4)
    c: Vertical(g5)
    c: PointOnObject(g6,g5)
    c: PointOnObject(g6,g4)
    c: Symmetric(g0,g1,g4)
    c: Symmetric(g0,g0,g5)
    c: PointOnObject(g5,g2)
    c: DistanceX(g0,g0) = 12.7
    c: DistanceY(g1,g1) = 75
    c: DistanceY(g-1,g0) = 25
    c: DistanceX(g-1,g5) = 10
    c: PointOnObject(g7,g5)
    c: PointOnObject(g8,g5)
    c: DistanceY(g7,g8) = 10
    c: DistanceY(g8,g6) = 22
    c: Coincident(g9,g8)
    c: Coincident(g10,g7)
    c: Diameter(g9) = 5
    c: Equal(g10,g9)
    c: Vertical(g12,g11)
    c: Equal(g11,g12)
    c: Equal(g12,g10)
    c: Horizontal(g11,g9)
    c: Horizontal(g12,g10)
    c: PointOnObject(g13,g-1)
    c: DistanceX(g-1,g13) = 160
    c: DistanceX(g11,g13) = 10
FEATURE [PartDesign::Pocket] Pocket010
  BaseFeature = -> Pocket009
  Direction = (0,-1e-16,1)
  Length = 10
  Length2 = 5
  Placement = pos=(0,0,0) rot=(1,0,0;1.5708rad)
  Profile = -> Sketch009
  ReferenceAxis = -> Sketch009 [N_Axis]
  Type = 0
FEATURE [PartDesign::Pocket] Pocket011
  BaseFeature = -> Pocket010
  Direction = (0,1,2e-16)
  Length = 5
  Length2 = 5
  Placement = pos=(0,0,0) rot=(1,0,0;1.5708rad)
  Profile = -> Sketch005
  ReferenceAxis = -> Sketch005 [N_Axis]
  Type = 0
FEATURE [Sketcher::SketchObject] Sketch012
  ExternalGeometry = -> [Pocket011]
  FullyConstrained = true
  MapMode = 5
  Placement = pos=(9.19873,-5.31089,2.3e-15) rot=(0.694747,-0.186157,-0.694747;3.50969rad)
  Support = -> [Pocket011]
  sketch-geometry (2):
    g0: Circle CenterX=-115 CenterY=-70 CenterZ=0 NormalX=0 NormalY=0 NormalZ=1 AngleXU=0 Radius=6
    g1: GeomPoint X=-120 Y=-70 Z=0
  constraints (4):
    c: Diameter(g0) = 12
    c: Symmetric(g-3,g-3,g1)
    c: Horizontal(g0,g1)
    c: Distance(g0,g1) = 5
FEATURE [PartDesign::Pocket] Pocket012
  BaseFeature = -> Pocket011
  Direction = (0.866025,-0.5,2e-16)
  Length = 10
  Length2 = 5
  Placement = pos=(0,0,0) rot=(1,0,0;1.5708rad)
  Profile = -> Sketch012
  ReferenceAxis = -> Sketch012 [N_Axis]
  Type = 0
FEATURE [Sketcher::SketchObject] Sketch013
  ExternalGeometry = -> [Pocket012]
  FullyConstrained = true
  MapMode = 5
  Placement = pos=(9.19873,-5.31089,2.3e-15) rot=(0.694747,-0.186157,-0.694747;3.50969rad)
  Support = -> [Pocket012]
  sketch-geometry (3):
    g0: Circle CenterX=-107 CenterY=-52.5 CenterZ=0 NormalX=0 NormalY=0 NormalZ=1 AngleXU=0 Radius=2.75
    g1: Circle CenterX=-107 CenterY=-87.5 CenterZ=0 NormalX=0 NormalY=0 NormalZ=1 AngleXU=0 Radius=2.75
    g2: LineSegment StartX=-115 StartY=-70 StartZ=0 EndX=-75 EndY=-70 EndZ=0
  constraints (8):
    c: DistanceY(g1,g0) = 35
    c: Coincident(g2,g-3)
    c: Horizontal(g2)
    c: DistanceX(g2,g2) = 40
    c: Symmetric(g0,g1,g2)
    c: DistanceX(g2,g0) = 8
    c: Diameter(g0) = 5.5
    c: Equal(g1,g0)
FEATURE [PartDesign::Pocket] Pocket013
  BaseFeature = -> Pocket012
  Direction = (0.866025,-0.5,2e-16)
  Length = 5
  Length2 = 5
  Placement = pos=(0,0,0) rot=(1,0,0;1.5708rad)
  Profile = -> Sketch013
  ReferenceAxis = -> Sketch013 [N_Axis]
  Type = 0
FEATURE [Sketcher::SketchObject] Sketch015
  ExternalGeometry = -> [Pocket013]
  FullyConstrained = true
  MapMode = 5
  Placement = pos=(110.801,63.9711,-2.83e-14) rot=(0.694747,0.186157,0.694747;3.50969rad)
  Support = -> [Pocket013]
  sketch-geometry (2):
    g0: Circle CenterX=115 CenterY=10 CenterZ=0 NormalX=0 NormalY=0 NormalZ=1 AngleXU=0 Radius=6
    g1: LineSegment StartX=120 StartY=10 StartZ=0 EndX=115 EndY=10 EndZ=0
  constraints (5):
    c: Diameter(g0) = 12
    c: Horizontal(g1)
    c: Symmetric(g-3,g-3,g1)
    c: DistanceX(g1,g1) = 5
    c: Coincident(g0,g1)
FEATURE [PartDesign::Pocket] Pocket014
  BaseFeature = -> Pocket013
  Direction = (-0.866025,-0.5,2e-16)
  Length = 10
  Length2 = 5
  Placement = pos=(0,0,0) rot=(1,0,0;1.5708rad)
  Profile = -> Sketch015
  ReferenceAxis = -> Sketch015 [N_Axis]
  Type = 0
FEATURE [Sketcher::SketchObject] Sketch016
  ExternalGeometry = -> [Pocket014]
  FullyConstrained = true
  MapMode = 5
  Placement = pos=(110.801,63.9711,-2.83e-14) rot=(0.694747,0.186157,0.694747;3.50969rad)
  Support = -> [Pocket014]
  sketch-geometry (3):
    g0: Circle CenterX=107 CenterY=27.5 CenterZ=0 NormalX=0 NormalY=0 NormalZ=1 AngleXU=0 Radius=2.75
    g1: Circle CenterX=107 CenterY=-7.5 CenterZ=0 NormalX=0 NormalY=0 NormalZ=1 AngleXU=0 Radius=2.75
    g2: LineSegment StartX=115 StartY=10 StartZ=0 EndX=103 EndY=10 EndZ=0
  constraints (8):
    c: Coincident(g2,g-3)
    c: Horizontal(g2)
    c: Distance(g2) = 12
    c: Symmetric(g0,g1,g2)
    c: Distance(g0,g1) = 35
    c: DistanceX(g1,g2) = 8
    c: Equal(g0,g1)
    c: Diameter(g1) = 5.5
FEATURE [PartDesign::Pocket] Pocket015
  BaseFeature = -> Pocket014
  Direction = (-0.866025,-0.5,2e-16)
  Length = 5
  Length2 = 5
  Placement = pos=(0,0,0) rot=(1,0,0;1.5708rad)
  Profile = -> Sketch016
  ReferenceAxis = -> Sketch016 [N_Axis]
  Type = 0
FEATURE [PartDesign::CoordinateSystem] LCS_0
  AttacherType = Attacher::AttachEngine3D
  MapMode = 2
  Support = -> [X_Axis001]
FEATURE [PartDesign::CoordinateSystem] LCS_1  label="LCS_motor1"
  AttacherType = Attacher::AttachEngine3D
  MapMode = 11
  Placement = pos=(124.551,40.1554,107) rot=(-0.774597,0.447214,-0.447214;1.82348rad)
  Support = -> [Pocket015]
FEATURE [PartDesign::CoordinateSystem] LCS_2  label="LCS_motor2"
  AttacherType = Attacher::AttachEngine3D
  MapMode = 11
  Placement = pos=(52.9487,70.4663,107) rot=(-0.377964,0.654654,0.654654;3.86433rad)
  Support = -> [Pocket015]
FEATURE [PartDesign::CoordinateSystem] LCS_3  label="LCS_camera"
  AttacherType = Attacher::AttachEngine3D
  MapMode = 45
  Placement = pos=(80,100,61) rot=(-1,0,0;1.5708rad)
  Support = -> [Pocket015]
FEATURE [PartDesign::CoordinateSystem] LCS_4  label="LCS_load1"
  AttacherType = Attacher::AttachEngine3D
  MapMode = 11
  Placement = pos=(10,34.5,14) rot=(0.707107,-0.707107,0;3.14159rad)
  Support = -> [Pocket015]
FEATURE [PartDesign::CoordinateSystem] LCS_5  label="LCS_load2"
  AttacherType = Attacher::AttachEngine3D
  MapMode = 11
  Placement = pos=(150,34.5,14) rot=(0.707107,-0.707107,0;3.14159rad)
  Support = -> [Pocket015]
FEATURE [PartDesign::CoordinateSystem] LCS_chute
  AttacherType = Attacher::AttachEngine3D
  MapMode = 45
  Placement = pos=(80,69.282,120) rot=(0.57735,0.57735,0.57735;2.0944rad)
  Support = -> [Pocket015]
FEATURE [PartDesign::CoordinateSystem] LCS_roof
  AttacherType = Attacher::AttachEngine3D
  MapMode = 1
  Placement = pos=(80,154,200) rot=(0,0,1;0rad)
  Support = -> [Pocket015]
FEATURE [PartDesign::CoordinateSystem] LCS_load2  label="LCS_load004"
  AttacherType = Attacher::AttachEngine3D
  MapMode = 11
  Placement = pos=(10,34.5,14) rot=(0.707107,-0.707107,0;3.14159rad)
  Support = -> [Pocket015]
FEATURE [Sketcher::SketchObject] Sketch017
  FullyConstrained = true
  MapMode = 5
  Placement = pos=(154,0,0) rot=(0.707107,0,-0.707107;3.14159rad)
  Support = -> [Pocket015]
  sketch-geometry (8):
    g0: LineSegment StartX=-6 StartY=-156 StartZ=0 EndX=-18 EndY=-156 EndZ=0
    g1: LineSegment StartX=-18 StartY=-156 StartZ=0 EndX=-18 EndY=-144 EndZ=0
    g2: LineSegment StartX=-18 StartY=-144 StartZ=0 EndX=-6 EndY=-144 EndZ=0
    g3: LineSegment StartX=-6 StartY=-144 StartZ=0 EndX=-6 EndY=-156 EndZ=0
    g4: LineSegment StartX=-133 StartY=-156 StartZ=0 EndX=-145 EndY=-156 EndZ=0
    g5: LineSegment StartX=-145 StartY=-156 StartZ=0 EndX=-145 EndY=-144 EndZ=0
    g6: LineSegment StartX=-145 StartY=-144 StartZ=0 EndX=-133 EndY=-144 EndZ=0
    g7: LineSegment StartX=-133 StartY=-144 StartZ=0 EndX=-133 EndY=-156 EndZ=0
  constraints (24):
    c: Coincident(g0,g1)
    c: Coincident(g1,g2)
    c: Coincident(g2,g3)
    c: Coincident(g3,g0)
    c: Horizontal(g0)
    c: Horizontal(g2)
    c: Vertical(g1)
    c: Vertical(g3)
    c: Coincident(g4,g5)
    c: Coincident(g5,g6)
    c: Coincident(g6,g7)
    c: Coincident(g7,g4)
    c: Horizontal(g4)
    c: Horizontal(g6)
    c: Vertical(g5)
    c: Vertical(g7)
    c: DistanceX(g0,g-1) = 6
    c: DistanceY(g1,g1) = 12
    c: Equal(g7,g1)
    c: Horizontal(g0,g4)
    c: Equal(g6,g2)
    c: DistanceX(g2,g2) = 12
    c: DistanceX(g4,g0) = 115
    c: DistanceY(g0,g-1) = 156
FEATURE [PartDesign::Pad] Pad003
  BaseFeature = -> Pocket015
  Direction = (-1,0,-2e-16)
  Length = 12
  Length2 = 10
  Placement = pos=(0,0,0) rot=(1,0,0;1.5708rad)
  Profile = -> Sketch017
  ReferenceAxis = -> Sketch017 [N_Axis]
  Type = 0
FEATURE [Sketcher::SketchObject] Sketch018
  FullyConstrained = true
  MapMode = 5
  Placement = pos=(6,0,0) rot=(0.707107,0,0.707107;3.14159rad)
  Support = -> [Pad003]
  sketch-geometry (8):
    g0: LineSegment StartX=6 StartY=-156 StartZ=0 EndX=18 EndY=-156 EndZ=0
    g1: LineSegment StartX=18 StartY=-156 StartZ=0 EndX=18 EndY=-144 EndZ=0
    g2: LineSegment StartX=18 StartY=-144 StartZ=0 EndX=6 EndY=-144 EndZ=0
    g3: LineSegment StartX=6 StartY=-144 StartZ=0 EndX=6 EndY=-156 EndZ=0
    g4: LineSegment StartX=133 StartY=-156 StartZ=0 EndX=145 EndY=-156 EndZ=0
    g5: LineSegment StartX=145 StartY=-156 StartZ=0 EndX=145 EndY=-144 EndZ=0
    g6: LineSegment StartX=145 StartY=-144 StartZ=0 EndX=133 EndY=-144 EndZ=0
    g7: LineSegment StartX=133 StartY=-144 StartZ=0 EndX=133 EndY=-156 EndZ=0
  constraints (24):
    c: Coincident(g0,g1)
    c: Coincident(g1,g2)
    c: Coincident(g2,g3)
    c: Coincident(g3,g0)
    c: Horizontal(g0)
    c: Horizontal(g2)
    c: Vertical(g1)
    c: Vertical(g3)
    c: Coincident(g4,g5)
    c: Coincident(g5,g6)
    c: Coincident(g6,g7)
    c: Coincident(g7,g4)
    c: Horizontal(g4)
    c: Horizontal(g6)
    c: Vertical(g5)
    c: Vertical(g7)
    c: Equal(g7,g1)
    c: Equal(g2,g6)
    c: DistanceX(g4,g4) = 12
    c: DistanceY(g7,g7) = 12
    c: DistanceX(g0,g4) = 115
    c: Horizontal(g0,g4)
    c: DistanceY(g0,g-1) = 156
    c: DistanceX(g-1,g0) = 6
FEATURE [PartDesign::Pad] Pad004
  BaseFeature = -> Pad003
  Direction = (1,0,-2e-16)
  Length = 12
  Length2 = 10
  Placement = pos=(0,0,0) rot=(1,0,0;1.5708rad)
  Profile = -> Sketch018
  ReferenceAxis = -> Sketch018 [N_Axis]
  Type = 0
FEATURE [Sketcher::SketchObject] Sketch019
  FullyConstrained = true
  MapMode = 5
  Placement = pos=(0,156,-3.46e-14) rot=(-1,0,0;1.5708rad)
  Support = -> [Pad004]
  sketch-geometry (8):
    g0: LineSegment StartX=12 StartY=-12 StartZ=0 EndX=148 EndY=-12 EndZ=0
    g1: LineSegment StartX=148 StartY=-12 StartZ=0 EndX=148 EndY=-139 EndZ=0
    g2: LineSegment StartX=148 StartY=-139 StartZ=0 EndX=12 EndY=-139 EndZ=0
    g3: LineSegment StartX=12 StartY=-139 StartZ=0 EndX=12 EndY=-12 EndZ=0
    g4: Circle CenterX=148 CenterY=-12 CenterZ=0 NormalX=0 NormalY=0 NormalZ=1 AngleXU=0 Radius=2.75
    g5: Circle CenterX=148 CenterY=-139 CenterZ=0 NormalX=0 NormalY=0 NormalZ=1 AngleXU=0 Radius=2.75
    g6: Circle CenterX=12 CenterY=-139 CenterZ=0 NormalX=0 NormalY=0 NormalZ=1 AngleXU=0 Radius=2.75
    g7: Circle CenterX=12 CenterY=-12 CenterZ=0 NormalX=0 NormalY=0 NormalZ=1 AngleXU=0 Radius=2.75
  constraints (20):
    c: Coincident(g0,g1)
    c: Coincident(g1,g2)
    c: Coincident(g2,g3)
    c: Coincident(g3,g0)
    c: Horizontal(g0)
    c: Horizontal(g2)
    c: Vertical(g1)
    c: Vertical(g3)
    c: Coincident(g4,g0)
    c: Coincident(g5,g1)
    c: Coincident(g6,g2)
    c: Coincident(g7,g0)
    c: Equal(g7,g4)
    c: Equal(g4,g5)
    c: Equal(g5,g6)
    c: Diameter(g4) = 5.5
    c: DistanceY(g7,g-1) = 12
    c: DistanceX(g-1,g7) = 12
    c: DistanceX(g0,g0) = 136
    c: DistanceY(g3,g3) = 127
FEATURE [PartDesign::Pocket] Pocket016
  BaseFeature = -> Pad004
  Direction = (0,-1,-2e-16)
  Length = 9
  Length2 = 5
  Placement = pos=(0,0,0) rot=(1,0,0;1.5708rad)
  Profile = -> Sketch019
  ReferenceAxis = -> Sketch019 [N_Axis]
  Type = 0
FEATURE [PartDesign::CoordinateSystem] LCS_back_panel
  AttacherType = Attacher::AttachEngine3D
  MapMode = 11
  Placement = pos=(12,156,12) rot=(0.57735,-0.57735,-0.57735;4.18879rad)
  Support = -> [Pocket016]
FEATURE [PartDesign::Fillet] Fillet
  Base = -> Pocket016 [Edge4,Edge3,Edge29,Edge34,Edge32,Edge31,Edge33,Edge35]
  BaseFeature = -> Pocket016
  Placement = pos=(0,0,0) rot=(1,0,0;1.5708rad)
  Radius = 1
  SupportTransform = false
  UseAllEdges = false
FEATURE [PartDesign::Body] Body
  Group = -> [Sketch,Pad,Sketch001,Pocket,Sketch002,Pad001,Sketch003,Pocket001,Sketch004,Pocket002,Sketch005,Sketch006,Pocket004,Sketch007,Pocket005,Sketch008,Pad002,Sketch009,Sketch010,Pocket008,Sketch011,Pocket009,Pocket010,Pocket011,Sketch012,Pocket012,Sketch013,Pocket013,Sketch015,Pocket014,Sketch016,Pocket015,Sketch017,Pad003,Sketch018,Pad004,Sketch019,Pocket016,Fillet]
  Origin = -> Origin
  Tip = -> Fillet
FEATURE [App::Part] house
  Group = -> [LCS_0,Body,LCS_1,LCS_2,LCS_3,LCS_4,LCS_5,LCS_chute,LCS_roof,LCS_load2,LCS_back_panel]
  Origin = -> Origin001
---- part load_cell.FCStd = doc fcstd_50da3ffad40b ----
FCSTD DOCUMENT  (FreeCAD 0.20R29177 +426 (Git))
Label: load_cell
License: All rights reserved
LicenseURL: http://en.wikipedia.org/wiki/All_rights_reserved
objects: PartDesign::CoordinateSystem×3, Sketcher::SketchObject×2, PartDesign::Pad×1, PartDesign::Pocket×1, PartDesign::Body×1, App::Part×1
note: 10 computed .brp shape members not serialized (recipe doc carries the construction recipe); baked Part::Feature solids carry a one-line shape summary decoded from their .brp

FEATURE [Sketcher::SketchObject] Sketch
  FullyConstrained = true
  MapMode = 5
  Support = -> [XY_Plane]
  sketch-geometry (10):
    g0: LineSegment StartX=0 StartY=0 StartZ=0 EndX=12.7 EndY=0 EndZ=0
    g1: LineSegment StartX=12.7 StartY=0 StartZ=0 EndX=12.7 EndY=75 EndZ=0
    g2: LineSegment StartX=12.7 StartY=75 StartZ=0 EndX=0 EndY=75 EndZ=0
    g3: LineSegment StartX=0 StartY=75 StartZ=0 EndX=0 EndY=0 EndZ=0
    g4: LineSegment StartX=6.35 StartY=75 StartZ=0 EndX=6.35 EndY=0 EndZ=0
    g5: Circle CenterX=6.35 CenterY=69.5 CenterZ=0 NormalX=0 NormalY=0 NormalZ=1 AngleXU=0 Radius=2
    g6: Circle CenterX=6.35 CenterY=59.5 CenterZ=0 NormalX=0 NormalY=0 NormalZ=1 AngleXU=0 Radius=2
    g7: Circle CenterX=6.35 CenterY=15.5 CenterZ=0 NormalX=0 NormalY=0 NormalZ=1 AngleXU=0 Radius=2
    g8: Circle CenterX=6.35 CenterY=5.5 CenterZ=0 NormalX=0 NormalY=0 NormalZ=1 AngleXU=0 Radius=2
    g9: GeomPoint X=6.35 Y=37.5 Z=0
  constraints (26):
    c: Coincident(g0,g1)
    c: Coincident(g1,g2)
    c: Coincident(g2,g3)
    c: Coincident(g3,g0)
    c: Horizontal(g0)
    c: Horizontal(g2)
    c: Vertical(g1)
    c: Vertical(g3)
    c: Coincident(g0,g-1)
    c: DistanceX(g2,g2) = 12.7
    c: DistanceY(g1,g1) = 75
    c: PointOnObject(g4,g2)
    c: PointOnObject(g4,g0)
    c: Symmetric(g0,g0,g4)
    c: PointOnObject(g5,g4)
    c: PointOnObject(g6,g4)
    c: PointOnObject(g8,g4)
    c: Equal(g8,g7)
    c: Equal(g7,g6)
    c: Equal(g6,g5)
    c: Diameter(g5) = 4
    c: DistanceY(g6,g5) = 10
    c: DistanceY(g8,g7) = 10
    c: DistanceY(g7,g6) = 44
    c: Symmetric(g4,g4,g9)
    c: Symmetric(g6,g7,g9)
FEATURE [PartDesign::Pad] Pad
  Direction = (0,0,1)
  Length = 12.7
  Length2 = 10
  Profile = -> Sketch
  ReferenceAxis = -> Sketch [N_Axis]
  Type = 0
FEATURE [Sketcher::SketchObject] Sketch001
  FullyConstrained = true
  MapMode = 5
  Placement = pos=(12.7,0,0) rot=(0.57735,0.57735,0.57735;2.0944rad)
  Support = -> [Pad]
  sketch-geometry (3):
    g0: GeomPoint X=37.5 Y=6.35 Z=0
    g1: ArcOfCircle CenterX=41 CenterY=6.35 CenterZ=0 NormalX=0 NormalY=0 NormalZ=1 AngleXU=0 Radius=4.94975 StartAngle=3.92699 EndAngle=8.63938
    g2: ArcOfCircle CenterX=34 CenterY=6.35 CenterZ=0 NormalX=0 NormalY=0 NormalZ=1 AngleXU=0 Radius=4.94975 StartAngle=0.785398 EndAngle=5.49779
  constraints (10):
    c: DistanceX(g-1,g0) = 37.5
    c: DistanceY(g0) = 6.35
    c: Coincident(g2,g1)
    c: Coincident(g2,g1)
    c: Equal(g1,g2)
    c: Horizontal(g0,g1)
    c: Horizontal(g1,g2)
    c: Vertical(g1,g0)
    c: Angle(g1) = 4.71239
    c: DistanceX(g2,g1) = 7
FEATURE [PartDesign::Pocket] Pocket
  BaseFeature = -> Pad
  Direction = (-1,0,0)
  Length = 5
  Length2 = 5
  Profile = -> Sketch001
  ReferenceAxis = -> Sketch001 [N_Axis]
  Type = 1
FEATURE [PartDesign::Body] Body
  Group = -> [Sketch,Pad,Sketch001,Pocket]
  Origin = -> Origin
  Tip = -> Pocket
FEATURE [PartDesign::CoordinateSystem] LCS_0
  AttacherType = Attacher::AttachEngine3D
  MapMode = 2
  Support = -> [X_Axis001]
FEATURE [PartDesign::CoordinateSystem] LCS_1
  AttacherType = Attacher::AttachEngine3D
  MapMode = 11
  Placement = pos=(6.35,59.5,12.7) rot=(0,0,1;1.5708rad)
  Support = -> [Pocket]
FEATURE [PartDesign::CoordinateSystem] LCS_2
  AttacherType = Attacher::AttachEngine3D
  MapMode = 11
  Placement = pos=(6.35,15.5,12.7) rot=(0,0,1;1.5708rad)
  Support = -> [Pocket]
FEATURE [App::Part] load_cell
  Group = -> [LCS_0,Body,LCS_1,LCS_2]
  Origin = -> Origin001
---- part perch.FCStd = doc fcstd_684e10caf35a ----
FCSTD DOCUMENT  (FreeCAD 0.20R29177 +426 (Git))
Label: perch
License: All rights reserved
LicenseURL: http://en.wikipedia.org/wiki/All_rights_reserved
objects: Sketcher::SketchObject×3, PartDesign::Pad×3, PartDesign::CoordinateSystem×2, PartDesign::Body×1, App::Part×1
note: 12 computed .brp shape members not serialized (recipe doc carries the construction recipe); baked Part::Feature solids carry a one-line shape summary decoded from their .brp

FEATURE [Sketcher::SketchObject] Sketch
  FullyConstrained = true
  MapMode = 5
  Support = -> [XY_Plane]
  sketch-geometry (7):
    g0: LineSegment StartX=0 StartY=0 StartZ=0 EndX=15 EndY=0 EndZ=0
    g1: LineSegment StartX=15 StartY=21 StartZ=0 EndX=0 EndY=21 EndZ=0
    g2: LineSegment StartX=0 StartY=21 StartZ=0 EndX=0 EndY=0 EndZ=0
    g3: Circle CenterX=6.35 CenterY=5.5 CenterZ=0 NormalX=0 NormalY=0 NormalZ=1 AngleXU=0 Radius=2.3
    g4: Circle CenterX=6.35 CenterY=15.5 CenterZ=0 NormalX=0 NormalY=0 NormalZ=1 AngleXU=0 Radius=2.3
    g5: GeomPoint X=8.65 Y=5.5 Z=0
    g6: LineSegment StartX=15 StartY=0 StartZ=0 EndX=15 EndY=21 EndZ=0
  constraints (19):
    c: Coincident(g1,g2)
    c: Coincident(g2,g0)
    c: Horizontal(g0)
    c: Horizontal(g1)
    c: Vertical(g2)
    c: Coincident(g0,g-1)
    c: DistanceY(g2,g2) = 21
    c: DistanceX(g1,g1) = 15
    c: PointOnObject(g5,g3)
    c: Horizontal(g5,g3)
    c: Equal(g4,g3)
    c: Diameter(g4) = 4.6
    c: Vertical(g4,g3)
    c: DistanceX(g0,g3) = 6.35
    c: DistanceY(g3,g4) = 10
    c: DistanceY(g0,g3) = 5.5
    c: Coincident(g6,g1)
    c: Vertical(g6)
    c: Coincident(g0,g6)
FEATURE [PartDesign::CoordinateSystem] LCS_0
  AttacherType = Attacher::AttachEngine3D
  MapMode = 2
  Support = -> [X_Axis001]
FEATURE [PartDesign::Pad] Pad
  Direction = (0,0,1)
  Length = 5
  Length2 = 10
  Profile = -> Sketch
  ReferenceAxis = -> Sketch [N_Axis]
  Type = 0
FEATURE [Sketcher::SketchObject] Sketch001
  FullyConstrained = true
  MapMode = 5
  Placement = pos=(15,0,0) rot=(0.57735,0.57735,0.57735;2.0944rad)
  Support = -> [Pad]
  sketch-geometry (1):
    g0: Circle CenterX=7.5 CenterY=-2.5 CenterZ=0 NormalX=0 NormalY=0 NormalZ=1 AngleXU=0 Radius=7.5
  constraints (3):
    c: Diameter(g0) = 15
    c: DistanceY(g0,g-1) = 2.5
    c: DistanceX(g-1,g0) = 7.5
FEATURE [PartDesign::Pad] Pad001
  BaseFeature = -> Pad
  Direction = (1,0,0)
  Length = 122.7
  Length2 = 10
  Profile = -> Sketch001
  ReferenceAxis = -> Sketch001 [N_Axis]
  Type = 0
FEATURE [Sketcher::SketchObject] Sketch002
  FullyConstrained = true
  MapMode = 5
  Support = -> [XY_Plane]
  expr: Constraints[11] = Sketch.Constraints[11]
  expr: Constraints[13] = Sketch.Constraints[13]
  expr: Constraints[14] = Sketch.Constraints[14]
  expr: Constraints[15] = Sketch.Constraints[15]
  expr: Constraints[25] = Sketch.Constraints[6]
  expr: Constraints[26] = Sketch.Constraints[7]
  expr: Constraints[30] = Sketch.Constraints[11]
  expr: Constraints[32] = Sketch.Constraints[13]
  expr: Constraints[33] = Sketch.Constraints[14]
  expr: Constraints[34] = Sketch.Constraints[15]
  expr: Constraints[44] = Sketch.Constraints[6]
  expr: Constraints[45] = Sketch.Constraints[7]
  expr: Constraints[49] = Sketch.Constraints[11]
  expr: Constraints[51] = Sketch.Constraints[13]
  expr: Constraints[52] = Sketch.Constraints[14]
  expr: Constraints[53] = Sketch.Constraints[15]
  expr: Constraints[63] = Sketch.Constraints[6]
  expr: Constraints[64] = Sketch.Constraints[7]
  expr: Constraints[68] = Sketch.Constraints[11]
  expr: Constraints[6] = Sketch.Constraints[6]
  expr: Constraints[70] = Sketch.Constraints[13]
  expr: Constraints[71] = Sketch.Constraints[14]
  expr: Constraints[72] = Sketch.Constraints[15]
  expr: Constraints[7] = Sketch.Constraints[7]
  expr: Constraints[82] = Sketch.Constraints[6]
  expr: Constraints[83] = Sketch.Constraints[7]
  expr: Constraints[87] = Sketch.Constraints[11]
  expr: Constraints[89] = Sketch.Constraints[13]
  expr: Constraints[90] = Sketch.Constraints[14]
  expr: Constraints[91] = Sketch.Constraints[15]
  sketch-geometry (41):
    g0: LineSegment StartX=0 StartY=0 StartZ=0 EndX=15 EndY=0 EndZ=0
    g1: LineSegment StartX=15 StartY=21 StartZ=0 EndX=0 EndY=21 EndZ=0
    g2: LineSegment StartX=0 StartY=21 StartZ=0 EndX=0 EndY=0 EndZ=0
    g3: Circle CenterX=6.35 CenterY=5.5 CenterZ=0 NormalX=0 NormalY=0 NormalZ=1 AngleXU=0 Radius=2.3
    g4: Circle CenterX=6.35 CenterY=15.5 CenterZ=0 NormalX=0 NormalY=0 NormalZ=1 AngleXU=0 Radius=2.3
    g5: GeomPoint X=8.65 Y=5.5 Z=0
    g6: LineSegment StartX=15 StartY=0 StartZ=0 EndX=15 EndY=21 EndZ=0
    g7: LineSegment StartX=0 StartY=0 StartZ=0 EndX=15 EndY=0 EndZ=0
    g8: LineSegment StartX=15 StartY=21 StartZ=0 EndX=0 EndY=21 EndZ=0
    g9: LineSegment StartX=0 StartY=21 StartZ=0 EndX=0 EndY=0 EndZ=0
    g10: Circle CenterX=6.35 CenterY=5.5 CenterZ=0 NormalX=0 NormalY=0 NormalZ=1 AngleXU=0 Radius=2.3
    g11: Circle CenterX=6.35 CenterY=15.5 CenterZ=0 NormalX=0 NormalY=0 NormalZ=1 AngleXU=0 Radius=2.3
    g12: GeomPoint X=8.65 Y=5.5 Z=0
    g13: LineSegment StartX=15 StartY=0 StartZ=0 EndX=15 EndY=21 EndZ=0
    g14: LineSegment StartX=0 StartY=0 StartZ=0 EndX=15 EndY=0 EndZ=0
    g15: LineSegment StartX=15 StartY=21 StartZ=0 EndX=0 EndY=21 EndZ=0
    g16: LineSegment StartX=0 StartY=21 StartZ=0 EndX=0 EndY=0 EndZ=0
    g17: Circle CenterX=6.35 CenterY=5.5 CenterZ=0 NormalX=0 NormalY=0 NormalZ=1 AngleXU=0 Radius=2.3
    g18: Circle CenterX=6.35 CenterY=15.5 CenterZ=0 NormalX=0 NormalY=0 NormalZ=1 AngleXU=0 Radius=2.3
    g19: GeomPoint X=8.65 Y=5.5 Z=0
    g20: LineSegment StartX=15 StartY=0 StartZ=0 EndX=15 EndY=21 EndZ=0
    g21: LineSegment StartX=0 StartY=0 StartZ=0 EndX=15 EndY=0 EndZ=0
    g22: LineSegment StartX=15 StartY=21 StartZ=0 EndX=0 EndY=21 EndZ=0
    g23: LineSegment StartX=0 StartY=21 StartZ=0 EndX=0 EndY=0 EndZ=0
    g24: Circle CenterX=6.35 CenterY=5.5 CenterZ=0 NormalX=0 NormalY=0 NormalZ=1 AngleXU=0 Radius=2.3
    g25: Circle CenterX=6.35 CenterY=15.5 CenterZ=0 NormalX=0 NormalY=0 NormalZ=1 AngleXU=0 Radius=2.3
    g26: GeomPoint X=8.65 Y=5.5 Z=0
    g27: LineSegment StartX=15 StartY=0 StartZ=0 EndX=15 EndY=21 EndZ=0
    g28: LineSegment StartX=0 StartY=0 StartZ=0 EndX=15 EndY=0 EndZ=0
    g29: LineSegment StartX=15 StartY=21 StartZ=0 EndX=0 EndY=21 EndZ=0
    g30: LineSegment StartX=0 StartY=21 StartZ=0 EndX=0 EndY=0 EndZ=0
    g31: Circle CenterX=6.35 CenterY=5.5 CenterZ=0 NormalX=0 NormalY=0 NormalZ=1 AngleXU=0 Radius=2.3
    g32: Circle CenterX=6.35 CenterY=15.5 CenterZ=0 NormalX=0 NormalY=0 NormalZ=1 AngleXU=0 Radius=2.3
    g33: GeomPoint X=8.65 Y=5.5 Z=0
    g34: LineSegment StartX=15 StartY=0 StartZ=0 EndX=15 EndY=21 EndZ=0
    g35: LineSegment StartX=152.7 StartY=0 StartZ=0 EndX=137.7 EndY=0 EndZ=0
    g36: LineSegment StartX=137.7 StartY=0 StartZ=0 EndX=137.7 EndY=21 EndZ=0
    g37: LineSegment StartX=137.7 StartY=21 StartZ=0 EndX=152.7 EndY=21 EndZ=0
    g38: LineSegment StartX=152.7 StartY=21 StartZ=0 EndX=152.7 EndY=0 EndZ=0
    g39: Circle CenterX=146.35 CenterY=5.5 CenterZ=0 NormalX=0 NormalY=0 NormalZ=1 AngleXU=0 Radius=2.3
    g40: Circle CenterX=146.35 CenterY=15.5 CenterZ=0 NormalX=0 NormalY=0 NormalZ=1 AngleXU=0 Radius=2.3
  constraints (113):
    c: Coincident(g1,g2)
    c: Coincident(g2,g0)
    c: Horizontal(g0)
    c: Horizontal(g1)
    c: Vertical(g2)
    c: Coincident(g0,g-1)
    c: DistanceY(g2,g2) = 21
    c: DistanceX(g1,g1) = 15
    c: PointOnObject(g5,g3)
    c: Horizontal(g5,g3)
    c: Equal(g4,g3)
    c: Diameter(g4) = 4.6
    c: Vertical(g4,g3)
    c: DistanceX(g0,g3) = 6.35
    c: DistanceY(g3,g4) = 10
    c: DistanceY(g0,g3) = 5.5
    c: Coincident(g6,g1)
    c: Vertical(g6)
    c: Coincident(g0,g6)
    c: Coincident(g8,g9)
    c: Coincident(g9,g7)
    c: Horizontal(g7)
    c: Horizontal(g8)
    c: Vertical(g9)
    c: Coincident(g7,g-1)
    c: DistanceY(g9,g9) = 21
    c: DistanceX(g8,g8) = 15
    c: PointOnObject(g12,g10)
    c: Horizontal(g12,g10)
    c: Equal(g11,g10)
    c: Diameter(g11) = 4.6
    c: Vertical(g11,g10)
    c: DistanceX(g7,g10) = 6.35
    c: DistanceY(g10,g11) = 10
    c: DistanceY(g7,g10) = 5.5
    c: Coincident(g13,g8)
    c: Vertical(g13)
    c: Coincident(g7,g13)
    c: Coincident(g15,g16)
    c: Coincident(g16,g14)
    c: Horizontal(g14)
    c: Horizontal(g15)
    c: Vertical(g16)
    c: Coincident(g14,g-1)
    c: DistanceY(g16,g16) = 21
    c: DistanceX(g15,g15) = 15
    c: PointOnObject(g19,g17)
    c: Horizontal(g19,g17)
    c: Equal(g18,g17)
    c: Diameter(g18) = 4.6
    c: Vertical(g18,g17)
    c: DistanceX(g14,g17) = 6.35
    c: DistanceY(g17,g18) = 10
    c: DistanceY(g14,g17) = 5.5
    c: Coincident(g20,g15)
    c: Vertical(g20)
    c: Coincident(g14,g20)
    c: Coincident(g22,g23)
    c: Coincident(g23,g21)
    c: Horizontal(g21)
    c: Horizontal(g22)
    c: Vertical(g23)
    c: Coincident(g21,g-1)
    c: DistanceY(g23,g23) = 21
    c: DistanceX(g22,g22) = 15
    c: PointOnObject(g26,g24)
    c: Horizontal(g26,g24)
    c: Equal(g25,g24)
    c: Diameter(g25) = 4.6
    c: Vertical(g25,g24)
    c: DistanceX(g21,g24) = 6.35
    c: DistanceY(g24,g25) = 10
    c: DistanceY(g21,g24) = 5.5
    c: Coincident(g27,g22)
    c: Vertical(g27)
    c: Coincident(g21,g27)
    c: Coincident(g29,g30)
    c: Coincident(g30,g28)
    c: Horizontal(g28)
    c: Horizontal(g29)
    c: Vertical(g30)
    c: Coincident(g28,g-1)
    c: DistanceY(g30,g30) = 21
    c: DistanceX(g29,g29) = 15
    c: PointOnObject(g33,g31)
    c: Horizontal(g33,g31)
    c: Equal(g32,g31)
    c: Diameter(g32) = 4.6
    c: Vertical(g32,g31)
    c: DistanceX(g28,g31) = 6.35
    c: DistanceY(g31,g32) = 10
    c: DistanceY(g28,g31) = 5.5
    c: Coincident(g34,g29)
    c: Vertical(g34)
    c: Coincident(g28,g34)
    c: Coincident(g35,g36)
    c: Coincident(g36,g37)
    c: Coincident(g37,g38)
    c: Coincident(g38,g35)
    c: Horizontal(g35)
    c: Horizontal(g37)
    c: Vertical(g36)
    c: Vertical(g38)
    c: PointOnObject(g35,g-1)
    c: Equal(g36,g6)
    c: Equal(g1,g37)
    c: Equal(g39,g40)
    c: Equal(g40,g3)
    c: Vertical(g40,g39)
    c: DistanceY(g39,g40) = 10
    c: DistanceY(g35,g39) = 5.5
    c: DistanceX(g39,g35) = 6.35
    c: DistanceX(g0,g35) = 152.7
FEATURE [PartDesign::Pad] Pad002
  BaseFeature = -> Pad001
  Direction = (0,0,1)
  Length = 5
  Length2 = 10
  Profile = -> Sketch002
  ReferenceAxis = -> Sketch002 [N_Axis]
  Type = 0
FEATURE [PartDesign::Body] Body
  Group = -> [Sketch,Pad,Sketch001,Pad001,Sketch002,Pad002]
  Origin = -> Origin
  Tip = -> Pad002
FEATURE [PartDesign::CoordinateSystem] LCS_1
  AttacherType = Attacher::AttachEngine3D
  MapMode = 11
  Placement = pos=(6.35,15.5,0) rot=(0,0,1;1.5708rad)
  Support = -> [Pad002]
FEATURE [App::Part] perch
  Group = -> [LCS_0,Body,LCS_1]
  Origin = -> Origin001
---- part roof.FCStd = doc fcstd_32953edb86e7 ----
FCSTD DOCUMENT  (FreeCAD 0.20R29177 +426 (Git))
Label: roof
License: All rights reserved
LicenseURL: http://en.wikipedia.org/wiki/All_rights_reserved
objects: Sketcher::SketchObject×3, PartDesign::Pad×2, PartDesign::CoordinateSystem×2, PartDesign::Mirrored×1, PartDesign::Body×1, App::Part×1
note: 11 computed .brp shape members not serialized (recipe doc carries the construction recipe); baked Part::Feature solids carry a one-line shape summary decoded from their .brp

FEATURE [Sketcher::SketchObject] Sketch
  FullyConstrained = true
  MapMode = 5
  Support = -> [XY_Plane]
  sketch-geometry (12):
    g0: LineSegment StartX=-73 StartY=7 StartZ=0 EndX=73 EndY=7 EndZ=0
    g1: LineSegment StartX=73 StartY=7 StartZ=0 EndX=73 EndY=153 EndZ=0
    g2: LineSegment StartX=73 StartY=153 StartZ=0 EndX=-73 EndY=153 EndZ=0
    g3: LineSegment StartX=-73 StartY=153 StartZ=0 EndX=-73 EndY=7 EndZ=0
    g4: LineSegment StartX=-69 StartY=11 StartZ=0 EndX=69 EndY=11 EndZ=0
    g5: LineSegment StartX=69 StartY=11 StartZ=0 EndX=69 EndY=149 EndZ=0
    g6: LineSegment StartX=69 StartY=149 StartZ=0 EndX=-69 EndY=149 EndZ=0
    g7: LineSegment StartX=-69 StartY=149 StartZ=0 EndX=-69 EndY=11 EndZ=0
    g8: LineSegment StartX=-69 StartY=11 StartZ=0 EndX=-73 EndY=11 EndZ=0
    g9: LineSegment StartX=-69 StartY=11 StartZ=0 EndX=-69 EndY=7 EndZ=0
    g10: LineSegment StartX=69 StartY=149 StartZ=0 EndX=69 EndY=153 EndZ=0
    g11: LineSegment StartX=69 StartY=149 StartZ=0 EndX=73 EndY=149 EndZ=0
  constraints (35):
    c: Coincident(g0,g1)
    c: Coincident(g2,g3)
    c: Horizontal(g2)
    c: Vertical(g1)
    c: Vertical(g3)
    c: Coincident(g4,g5)
    c: Coincident(g5,g6)
    c: Coincident(g6,g7)
    c: Coincident(g7,g4)
    c: Horizontal(g4)
    c: Horizontal(g6)
    c: Vertical(g5)
    c: Vertical(g7)
    c: Coincident(g8,g4)
    c: Horizontal(g8)
    c: Coincident(g9,g4)
    c: PointOnObject(g9,g0)
    c: PointOnObject(g8,g3)
    c: Vertical(g9)
    c: Coincident(g10,g5)
    c: PointOnObject(g10,g2)
    c: Vertical(g10)
    c: Coincident(g11,g5)
    c: PointOnObject(g11,g1)
    c: Horizontal(g11)
    c: Equal(g11,g10)
    c: Equal(g10,g9)
    c: Equal(g9,g8)
    c: DistanceX(g11,g11) = 4
    c: DistanceX(g2,g2) = 146
    c: Equal(g2,g3)
    c: Coincident(g0,g3)
    c: Coincident(g1,g2)
    c: Symmetric(g0,g0,g-2)
    c: DistanceY(g-1,g0) = 7
FEATURE [Sketcher::SketchObject] Sketch001
  AttachmentOffset = pos=(0,0,20) rot=(0,0,1;0rad)
  FullyConstrained = true
  MapMode = 5
  Placement = pos=(0,-20,-4.4e-15) rot=(1,0,0;1.5708rad)
  Support = -> [XZ_Plane]
  sketch-geometry (6):
    g0: LineSegment StartX=0 StartY=25 StartZ=0 EndX=-90 EndY=2.50041 EndZ=0
    g1: LineSegment StartX=0 StartY=25 StartZ=0 EndX=90 EndY=2.50041 EndZ=0
    g2: LineSegment StartX=90 StartY=2.50041 StartZ=0 EndX=90 EndY=-3.49959 EndZ=0
    g3: LineSegment StartX=90 StartY=-3.49959 StartZ=0 EndX=0 EndY=19 EndZ=0
    g4: LineSegment StartX=0 StartY=19 StartZ=0 EndX=-90 EndY=-3.49959 EndZ=0
    g5: LineSegment StartX=-90 StartY=-3.49959 StartZ=0 EndX=-90 EndY=2.50041 EndZ=0
  constraints (17):
    c: PointOnObject(g0,g-2)
    c: Coincident(g1,g0)
    c: Coincident(g2,g1)
    c: Coincident(g3,g2)
    c: PointOnObject(g3,g-2)
    c: Coincident(g4,g3)
    c: Coincident(g5,g4)
    c: Coincident(g5,g0)
    c: Parallel(g4,g0)
    c: Parallel(g3,g1)
    c: Equal(g3,g1)
    c: Equal(g4,g0)
    c: Symmetric(g4,g2,g-2)
    c: DistanceX(g4,g2) = 180
    c: DistanceY(g2,g2) = 6
    c: Angle(g-1,g0) = 0.244974
    c: DistanceY(g-1,g3) = 19
FEATURE [PartDesign::Pad] Pad
  Direction = (0,-1,2e-16)
  Length = 200
  Length2 = 10
  Placement = pos=(0,0,0) rot=(1,0,0;1.5708rad)
  Profile = -> Sketch001
  ReferenceAxis = -> Sketch001 [N_Axis]
  Reversed = true
  Type = 0
FEATURE [Sketcher::SketchObject] Sketch002
  FullyConstrained = true
  MapMode = 5
  Support = -> [XY_Plane]
  sketch-geometry (9):
    g0: LineSegment StartX=0 StartY=7 StartZ=0 EndX=73 EndY=7 EndZ=0
    g1: LineSegment StartX=73 StartY=7 StartZ=0 EndX=73 EndY=153 EndZ=0
    g2: LineSegment StartX=73 StartY=153 StartZ=0 EndX=0 EndY=153 EndZ=0
    g3: LineSegment StartX=0 StartY=11 StartZ=0 EndX=69 EndY=11 EndZ=0
    g4: LineSegment StartX=69 StartY=11 StartZ=0 EndX=69 EndY=149 EndZ=0
    g5: LineSegment StartX=69 StartY=149 StartZ=0 EndX=0 EndY=149 EndZ=0
    g6: LineSegment StartX=69 StartY=149 StartZ=0 EndX=73 EndY=149 EndZ=0
    g7: LineSegment StartX=0 StartY=149 StartZ=0 EndX=0 EndY=153 EndZ=0
    g8: LineSegment StartX=0 StartY=11 StartZ=0 EndX=0 EndY=7 EndZ=0
  constraints (27):
    c: Coincident(g0,g1)
    c: Horizontal(g2)
    c: Vertical(g1)
    c: Coincident(g3,g4)
    c: Coincident(g4,g5)
    c: Horizontal(g3)
    c: Horizontal(g5)
    c: Vertical(g4)
    c: Coincident(g6,g4)
    c: PointOnObject(g6,g1)
    c: Horizontal(g6)
    c: Coincident(g1,g2)
    c: Coincident(g7,g5)
    c: Coincident(g7,g2)
    c: Coincident(g8,g3)
    c: Coincident(g8,g0)
    c: Vertical(g8)
    c: Vertical(g7)
    c: Vertical(g7,g3)
    c: Equal(g6,g7)
    c: Equal(g7,g8)
    c: DistanceX(g6,g6) = 4
    c: DistanceY(g-1,g0) = 7
    c: PointOnObject(g0,g-2)
    c: DistanceX(g2,g2) = 73
    c: Horizontal(g0)
    c: DistanceY(g1,g1) = 146
FEATURE [PartDesign::Pad] Pad001
  BaseFeature = -> Pad
  Direction = (0,0,1)
  Length = 10
  Length2 = 10
  Placement = pos=(0,0,0) rot=(1,0,0;1.5708rad)
  Profile = -> Sketch002
  ReferenceAxis = -> Sketch002 [N_Axis]
  Type = 2
FEATURE [PartDesign::Mirrored] Mirrored
  BaseFeature = -> Pad001
  MirrorPlane = -> Sketch002 [V_Axis]
  Originals = -> [Pad001]
  Placement = pos=(0,0,0) rot=(1,0,0;1.5708rad)
FEATURE [PartDesign::Body] Body
  Group = -> [Sketch,Sketch001,Pad,Sketch002,Pad001,Mirrored]
  Origin = -> Origin
  Tip = -> Mirrored
FEATURE [PartDesign::CoordinateSystem] LCS_0
  AttacherType = Attacher::AttachEngine3D
  MapMode = 2
  Support = -> [X_Axis001]
FEATURE [PartDesign::CoordinateSystem] LCS_1
  AttacherType = Attacher::AttachEngine3D
  MapMode = 1
  Placement = pos=(0,7,19) rot=(0,0,1;0rad)
  Support = -> [Mirrored]
FEATURE [App::Part] roof
  Group = -> [LCS_0,Body,LCS_1]
  Origin = -> Origin001
---- part seed_chute.FCStd = doc fcstd_e36a9d2b5479 ----
FCSTD DOCUMENT  (FreeCAD 0.20R29177 +426 (Git))
Label: seed_chute
License: All rights reserved
LicenseURL: http://en.wikipedia.org/wiki/All_rights_reserved
objects: Sketcher::SketchObject×7, PartDesign::Mirrored×3, PartDesign::AdditiveLoft×1, PartDesign::SubtractiveLoft×1, PartDesign::Pad×1, PartDesign::Pocket×1, PartDesign::Chamfer×1, PartDesign::Body×1, PartDesign::CoordinateSystem×1, App::Part×1
note: 22 computed .brp shape members not serialized (recipe doc carries the construction recipe); baked Part::Feature solids carry a one-line shape summary decoded from their .brp

FEATURE [Sketcher::SketchObject] Sketch  label="base_out"
  FullyConstrained = true
  MapMode = 5
  Support = -> [XY_Plane]
  sketch-geometry (12):
    g0: LineSegment StartX=-4.27745 StartY=6.76795 StartZ=0 EndX=-20.7319 EndY=-2.73205 EndZ=0
    g1: LineSegment StartX=-20.7319 StartY=-2.73205 StartZ=0 EndX=-42.7319 EndY=35.3731 EndZ=0
    g2: LineSegment StartX=-42.7319 StartY=35.3731 StartZ=0 EndX=-26.2774 EndY=44.8731 EndZ=0
    g3: LineSegment StartX=-26.2774 StartY=44.8731 StartZ=0 EndX=-4.27745 EndY=6.76795 EndZ=0
    g4: LineSegment StartX=-27.0095 StartY=42.141 StartZ=0 EndX=-39.9999 EndY=34.641 EndZ=0
    g5: LineSegment StartX=-39.9999 StartY=34.641 StartZ=0 EndX=-19.9999 EndY=0 EndZ=0
    g6: LineSegment StartX=-19.9999 StartY=0 StartZ=0 EndX=-7.0095 EndY=7.5 EndZ=0
    g7: LineSegment StartX=-7.0095 StartY=7.5 StartZ=0 EndX=-27.0095 EndY=42.141 EndZ=0
    g8: LineSegment StartX=-27.0095 StartY=42.141 StartZ=0 EndX=-28.0095 EndY=43.8731 EndZ=0
    g9: LineSegment StartX=-27.0095 StartY=42.141 StartZ=0 EndX=-25.2774 EndY=43.141 EndZ=0
    g10: LineSegment StartX=-19.9999 StartY=0 StartZ=0 EndX=-18.9999 EndY=-1.73205 EndZ=0
    g11: LineSegment StartX=-19.9999 StartY=0 StartZ=0 EndX=-21.7319 EndY=-1 EndZ=0
  constraints (36):
    c: Coincident(g1,g0)
    c: Coincident(g2,g1)
    c: Coincident(g3,g2)
    c: Coincident(g3,g0)
    c: Parallel(g1,g3)
    c: Parallel(g0,g2)
    c: Perpendicular(g3,g0)
    c: Angle(g-1,g1) = 2.0944
    c: Coincident(g5,g4)
    c: Coincident(g6,g5)
    c: Coincident(g7,g6)
    c: Coincident(g7,g4)
    c: DistanceX(g6,g-1) = 7.0095
    c: Parallel(g6,g0)
    c: Parallel(g6,g4)
    c: Parallel(g5,g7)
    c: Perpendicular(g4,g7)
    c: PointOnObject(g5,g-1)
    c: Coincident(g8,g4)
    c: PointOnObject(g8,g2)
    c: Coincident(g9,g4)
    c: PointOnObject(g9,g3)
    c: Coincident(g10,g5)
    c: PointOnObject(g10,g0)
    c: Coincident(g11,g5)
    c: PointOnObject(g11,g1)
    c: Perpendicular(g5,g11)
    c: Perpendicular(g6,g10)
    c: Perpendicular(g7,g9)
    c: Perpendicular(g8,g4)
    c: Equal(g9,g8)
    c: Equal(g8,g10)
    c: Equal(g10,g11)
    c: Distance(g11) = 2
    c: Distance(g6) = 15
    c: Distance(g7) = 40
FEATURE [Sketcher::SketchObject] Sketch001  label="mid_rect"
  AttachmentOffset = pos=(0,0,15) rot=(0,0,1;0rad)
  FullyConstrained = true
  MapMode = 5
  Placement = pos=(0,0,15) rot=(0,0,1;0rad)
  Support = -> [XY_Plane]
  sketch-geometry (4):
    g0: LineSegment StartX=0 StartY=7.5 StartZ=0 EndX=-23.3827 EndY=-6 EndZ=0
    g1: LineSegment StartX=-23.3827 StartY=-6 StartZ=0 EndX=-48.3827 EndY=37.3013 EndZ=0
    g2: LineSegment StartX=-48.3827 StartY=37.3013 StartZ=0 EndX=-25 EndY=50.8013 EndZ=0
    g3: LineSegment StartX=-25 StartY=50.8013 StartZ=0 EndX=0 EndY=7.5 EndZ=0
  constraints (12):
    c: Coincident(g1,g0)
    c: Coincident(g2,g1)
    c: Coincident(g3,g2)
    c: Coincident(g3,g0)
    c: Perpendicular(g3,g0)
    c: Parallel(g3,g1)
    c: Parallel(g0,g2)
    c: Angle(g-1,g1) = 2.0944
    c: PointOnObject(g0,g-2)
    c: Distance(g0) = 27
    c: Distance(g3) = 50
    c: DistanceY(g-1,g0) = 7.5
FEATURE [Sketcher::SketchObject] Sketch002  label="semifinal_out"
  AttachmentOffset = pos=(0,0,30) rot=(0,0,1;0rad)
  FullyConstrained = true
  MapMode = 5
  Placement = pos=(0,0,30) rot=(0,0,1;0rad)
  Support = -> [XY_Plane]
  sketch-geometry (4):
    g0: LineSegment StartX=-73.5 StartY=62.782 StartZ=0 EndX=0 EndY=62.782 EndZ=0
    g1: LineSegment StartX=0 StartY=62.782 StartZ=0 EndX=0 EndY=-84.218 EndZ=0
    g2: LineSegment StartX=0 StartY=-84.218 StartZ=0 EndX=-73.5 EndY=-84.218 EndZ=0
    g3: LineSegment StartX=-73.5 StartY=-84.218 StartZ=0 EndX=-73.5 EndY=62.782 EndZ=0
  constraints (12):
    c: Coincident(g0,g1)
    c: Coincident(g1,g2)
    c: Coincident(g2,g3)
    c: Coincident(g3,g0)
    c: Horizontal(g0)
    c: Horizontal(g2)
    c: Vertical(g1)
    c: Vertical(g3)
    c: DistanceY(g3,g3) = 147
    c: PointOnObject(g1,g-2)
    c: DistanceX(g2,g2) = 73.5
    c: DistanceY(g-1,g0) = 62.782
FEATURE [Sketcher::SketchObject] Sketch003  label="mid_ellipse_out"
  AttachmentOffset = pos=(0,0,15) rot=(0,0,1;0rad)
  FullyConstrained = true
  MapMode = 5
  Placement = pos=(0,0,15) rot=(0,0,1;0rad)
  Support = -> [XY_Plane]
  sketch-geometry (5):
    g0: Ellipse CenterX=-23.1936 CenterY=20.2155 CenterZ=0 NormalX=0 NormalY=0 NormalZ=1 MajorRadius=30 MinorRadius=17.5 AngleXU=-1.0472
    g1: LineSegment StartX=-8.19358 StartY=-5.76524 StartZ=0 EndX=-38.1936 EndY=46.1963 EndZ=0
    g2: LineSegment StartX=-8.03814 StartY=28.9655 StartZ=0 EndX=-38.349 EndY=11.4655 EndZ=0
    g3: GeomPoint X=-11.0101 Y=-0.886906 Z=0
    g4: GeomPoint X=-35.3771 Y=41.318 Z=0
  constraints (6):
    c: InternalAlignment(g1-g4 -> g0) x4
    c: Angle(g-1,g1) = 2.0944
    c: Distance(g1) = 60
    c: DistanceX(g0) = -23.1936
    c: DistanceY(g0) = 20.2155
    c: Distance(g2) = 35
FEATURE [Sketcher::SketchObject] Sketch004  label="base_in"
  FullyConstrained = true
  MapMode = 5
  Support = -> [XY_Plane]
  sketch-geometry (4):
    g0: LineSegment StartX=-19.9999 StartY=0 StartZ=0 EndX=-7.0095 EndY=7.5 EndZ=0
    g1: LineSegment StartX=-7.0095 StartY=7.5 StartZ=0 EndX=-27.0095 EndY=42.141 EndZ=0
    g2: LineSegment StartX=-27.0095 StartY=42.141 StartZ=0 EndX=-39.9999 EndY=34.641 EndZ=0
    g3: LineSegment StartX=-39.9999 StartY=34.641 StartZ=0 EndX=-19.9999 EndY=0 EndZ=0
  constraints (12):
    c: PointOnObject(g0,g-1)
    c: Coincident(g2,g1)
    c: Coincident(g3,g2)
    c: Coincident(g3,g0)
    c: Coincident(g0,g1)
    c: Perpendicular(g1,g0)
    c: Parallel(g1,g3)
    c: Parallel(g2,g0)
    c: DistanceX(g0,g-1) = 7.0095
    c: Angle(g-1,g3) = 2.0944
    c: Distance(g0) = 15
    c: Distance(g1) = 40
FEATURE [Sketcher::SketchObject] Sketch005  label="mid_ellipse_in"
  AttachmentOffset = pos=(0,0,15) rot=(0,0,1;0rad)
  FullyConstrained = true
  MapMode = 5
  Placement = pos=(0,0,15) rot=(0,0,1;0rad)
  Support = -> [XY_Plane]
  expr: Constraints[4] = Sketch003.Constraints[4]
  expr: Constraints[5] = Sketch003.Constraints[5]
  expr: Constraints[6] = Sketch003.Constraints[6]
  expr: Constraints[7] = Sketch003.Constraints[7]
  expr: Constraints[8] = Sketch003.Constraints[8]
  sketch-geometry (10):
    g0: Ellipse CenterX=-23.1936 CenterY=20.2155 CenterZ=0 NormalX=0 NormalY=0 NormalZ=1 MajorRadius=30 MinorRadius=17.5 AngleXU=-1.0472
    g1: LineSegment StartX=-8.19358 StartY=-5.76524 StartZ=0 EndX=-38.1936 EndY=46.1963 EndZ=0
    g2: LineSegment StartX=-8.03814 StartY=28.9655 StartZ=0 EndX=-38.349 EndY=11.4655 EndZ=0
    g3: GeomPoint X=-11.0101 Y=-0.886906 Z=0
    g4: GeomPoint X=-35.3771 Y=41.318 Z=0
    g5: Ellipse CenterX=-23.1936 CenterY=20.2155 CenterZ=0 NormalX=0 NormalY=0 NormalZ=1 MajorRadius=28 MinorRadius=15.5 AngleXU=-1.0472
    g6: LineSegment StartX=-9.19358 StartY=-4.03319 StartZ=0 EndX=-37.1936 EndY=44.4642 EndZ=0
    g7: LineSegment StartX=-9.77019 StartY=27.9655 StartZ=0 EndX=-36.617 EndY=12.4655 EndZ=0
    g8: GeomPoint X=-11.5344 Y=0.021155 Z=0
    g9: GeomPoint X=-34.8528 Y=40.4099 Z=0
  constraints (11):
    c: InternalAlignment(g1-g4 -> g0) x4
    c: Angle(g-1,g1) = 2.0944
    c: Distance(g1) = 60
    c: DistanceX(g0) = -23.1936
    c: DistanceY(g0) = 20.2155
    c: Distance(g2) = 35
    c: InternalAlignment(g6-g9 -> g5) x4
    c: Coincident(g5,g0)
    c: PointOnObject(g6,g1)
    c: Distance(g7,g2) = 2
    c: Distance(g6,g1) = 2
FEATURE [Sketcher::SketchObject] Sketch006  label="semifinal_in"
  AttachmentOffset = pos=(0,0,30) rot=(0,0,1;0rad)
  FullyConstrained = true
  MapMode = 5
  Placement = pos=(0,0,30) rot=(0,0,1;0rad)
  Support = -> [XY_Plane]
  expr: Constraints[16] = Sketch002.Constraints[8]
  expr: Constraints[18] = Sketch002.Constraints[10]
  expr: Constraints[19] = Sketch002.Constraints[11]
  sketch-geometry (12):
    g0: LineSegment StartX=-71.5 StartY=60.782 StartZ=0 EndX=-2 EndY=60.782 EndZ=0
    g1: LineSegment StartX=-2 StartY=60.782 StartZ=0 EndX=-2 EndY=-82.218 EndZ=0
    g2: LineSegment StartX=-2 StartY=-82.218 StartZ=0 EndX=-71.5 EndY=-82.218 EndZ=0
    g3: LineSegment StartX=-71.5 StartY=-82.218 StartZ=0 EndX=-71.5 EndY=60.782 EndZ=0
    g4: LineSegment StartX=-73.5 StartY=62.782 StartZ=0 EndX=0 EndY=62.782 EndZ=0
    g5: LineSegment StartX=0 StartY=62.782 StartZ=0 EndX=0 EndY=-84.218 EndZ=0
    g6: LineSegment StartX=0 StartY=-84.218 StartZ=0 EndX=-73.5 EndY=-84.218 EndZ=0
    g7: LineSegment StartX=-73.5 StartY=-84.218 StartZ=0 EndX=-73.5 EndY=62.782 EndZ=0
    g8: LineSegment StartX=-71.5 StartY=60.782 StartZ=0 EndX=-71.5 EndY=62.782 EndZ=0
    g9: LineSegment StartX=-71.5 StartY=60.782 StartZ=0 EndX=-73.5 EndY=60.782 EndZ=0
    g10: LineSegment StartX=-2 StartY=-82.218 StartZ=0 EndX=-2 EndY=-84.218 EndZ=0
    g11: LineSegment StartX=-2 StartY=-82.218 StartZ=0 EndX=0 EndY=-82.218 EndZ=0
  constraints (36):
    c: Coincident(g0,g1)
    c: Coincident(g1,g2)
    c: Coincident(g2,g3)
    c: Coincident(g3,g0)
    c: Horizontal(g0)
    c: Horizontal(g2)
    c: Vertical(g1)
    c: Vertical(g3)
    c: Coincident(g4,g5)
    c: Coincident(g5,g6)
    c: Coincident(g6,g7)
    c: Coincident(g7,g4)
    c: Horizontal(g4)
    c: Horizontal(g6)
    c: Vertical(g5)
    c: Vertical(g7)
    c: DistanceY(g7,g7) = 147
    c: PointOnObject(g5,g-2)
    c: DistanceX(g6,g6) = 73.5
    c: DistanceY(g-1,g4) = 62.782
    c: Coincident(g8,g0)
    c: PointOnObject(g8,g4)
    c: Coincident(g9,g0)
    c: PointOnObject(g9,g7)
    c: Horizontal(g9)
    c: Vertical(g8)
    c: Coincident(g10,g1)
    c: PointOnObject(g10,g6)
    c: Vertical(g10)
    c: Coincident(g11,g1)
    c: PointOnObject(g11,g5)
    c: Horizontal(g11)
    c: Equal(g11,g10)
    c: Equal(g10,g9)
    c: Equal(g9,g8)
    c: DistanceY(g8,g8) = 2
FEATURE [PartDesign::AdditiveLoft] AdditiveLoft
  Closed = false
  Profile = -> Sketch
  Ruled = true
  Sections = -> [Sketch003,Sketch002]
FEATURE [PartDesign::SubtractiveLoft] SubtractiveLoft
  BaseFeature = -> AdditiveLoft
  Closed = false
  Profile = -> Sketch004
  Ruled = true
  Sections = -> [Sketch005,Sketch006]
FEATURE [PartDesign::Pad] Pad
  BaseFeature = -> SubtractiveLoft
  Direction = (0,0,1)
  Length = 30
  Length2 = 10
  Profile = -> SubtractiveLoft [Face38]
  Type = 0
FEATURE [PartDesign::Mirrored] Mirrored
  BaseFeature = -> Pad
  MirrorPlane = -> YZ_Plane
  Originals = -> [Pad]
FEATURE [PartDesign::Mirrored] Mirrored001
  BaseFeature = -> Mirrored
  MirrorPlane = -> Sketch [V_Axis]
  Originals = -> [AdditiveLoft]
FEATURE [PartDesign::Mirrored] Mirrored002
  BaseFeature = -> Mirrored001
  MirrorPlane = -> Sketch004 [V_Axis]
  Originals = -> [SubtractiveLoft]
FEATURE [PartDesign::Pocket] Pocket
  BaseFeature = -> Mirrored002
  Direction = (1,0,0)
  Length = 5
  Length2 = 5
  Profile = -> Mirrored002 [Face50,Face49,Face48]
  Type = 0
FEATURE [PartDesign::Chamfer] Chamfer
  Angle = 45
  Base = -> Pocket [Edge109,Edge107,Edge182,Edge195]
  BaseFeature = -> Pocket
  ChamferType = 0
  FlipDirection = false
  Size = 1
  Size2 = 1
  SupportTransform = false
  UseAllEdges = false
FEATURE [PartDesign::Body] Body
  Group = -> [Sketch,Sketch001,Sketch002,Sketch003,Sketch004,Sketch005,Sketch006,AdditiveLoft,SubtractiveLoft,Pad,Mirrored,Mirrored001,Mirrored002,Pocket,Chamfer]
  Origin = -> Origin
  Tip = -> Chamfer
FEATURE [PartDesign::CoordinateSystem] LCS_0
  AttacherType = Attacher::AttachEngine3D
  MapMode = 2
  Support = -> [X_Axis001]
FEATURE [App::Part] seed_chute
  Group = -> [LCS_0,Body]
  Origin = -> Origin001
